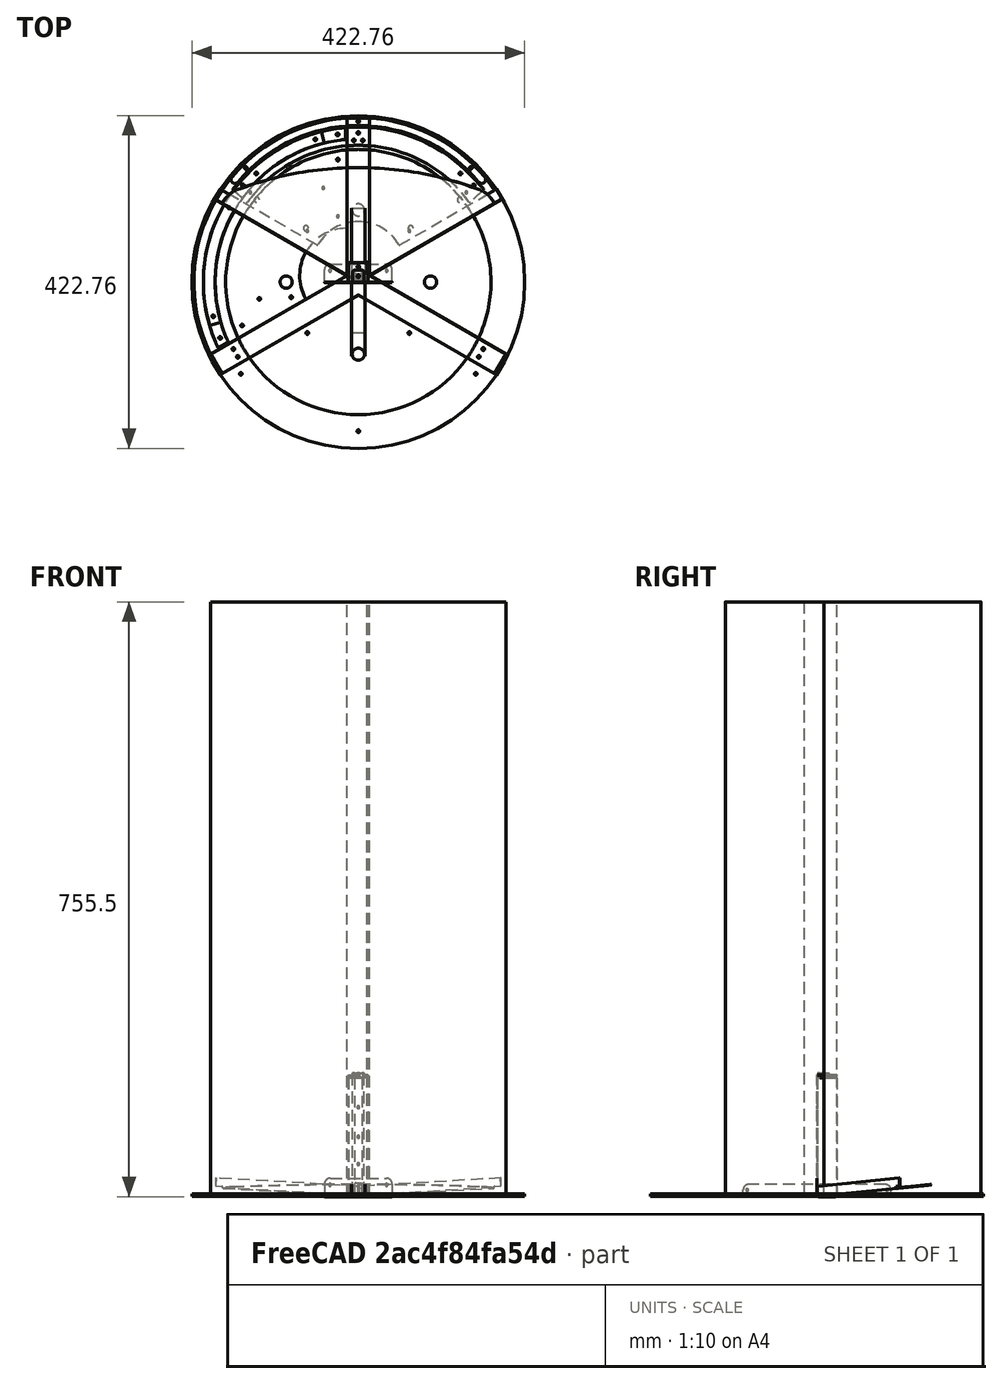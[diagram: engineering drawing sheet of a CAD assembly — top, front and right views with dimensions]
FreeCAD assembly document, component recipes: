
FREECAD ASSEMBLY — COMPONENT RECIPES ("composit_stand3-small")

This assembly document has 17 components, labeled P0..P16 below (a component is one placed body or linked part). 17 of them carry a construction recipe — the FreeCAD feature program that regenerates the part from scratch, quoted from this document or its linked companion documents; the rest are supplied as boundary geometry only. No exploded tour is included for this assembly.
NOTE — this tour is split across 2 documents so each fits a 32k-token context. This is document 1: the component sections continue in the remaining 1 document, each repeating the header above.
COMPONENT P0 — recipe-attached ("Body001_material_0.30ansi", modeled in this document).
Construction recipe (the document's own serialized feature program — sketch geometry with constraints, then the solid features built on it; lengths are millimeters unless a unit is written):

FEATURE [Sketcher::SketchObject] Sketch003
  FullyConstrained = true
  MapMode = 5
  Support = -> [XY_Plane001]
  sketch-geometry (13):
    g0: LineSegment StartX=-14.5 StartY=8.37158 StartZ=0 EndX=-14.5 EndY=208.372 EndZ=0
    g1: LineSegment StartX=-14.5 StartY=208.372 StartZ=0 EndX=14.5 EndY=208.372 EndZ=0
    g2: LineSegment StartX=187.705 StartY=-91.6284 StartZ=0 EndX=173.205 EndY=-116.743 EndZ=0
    g3: LineSegment StartX=173.205 StartY=-116.743 StartZ=0 EndX=0 EndY=-16.7432 EndZ=0
    g4: LineSegment StartX=0 StartY=-16.7432 StartZ=0 EndX=-173.205 EndY=-116.743 EndZ=0
    g5: LineSegment StartX=-173.205 StartY=-116.743 StartZ=0 EndX=-187.705 EndY=-91.6284 EndZ=0
    g6: LineSegment StartX=-187.705 StartY=-91.6284 StartZ=0 EndX=-14.5 EndY=8.37158 EndZ=0
    g7: LineSegment StartX=-14.5 StartY=8.37158 StartZ=0 EndX=0 EndY=0 EndZ=0
    g8: LineSegment StartX=0 StartY=0 StartZ=0 EndX=0 EndY=-16.7432 EndZ=0
    g9: LineSegment StartX=14.5 StartY=208.372 StartZ=0 EndX=14.5 EndY=8.97158 EndZ=0
    g10: LineSegment StartX=187.705 StartY=-91.6284 StartZ=0 EndX=11.5 EndY=10.1036 EndZ=0
    g11: LineSegment StartX=11.5 StartY=10.1036 StartZ=0 EndX=11.5 EndY=25.1036 EndZ=0
    g12: LineSegment StartX=0 StartY=0 StartZ=0 EndX=14.5 EndY=8.37158 EndZ=0
  constraints (40):
    c: Vertical(g0)
    c: Coincident(g0,g1)
    c: Coincident(g2,g3)
    c: PointOnObject(g3,g-2)
    c: Coincident(g3,g4)
    c: Coincident(g4,g5)
    c: Coincident(g6,g5)
    c: Equal(g4,g3)
    c: Equal(g2,g5)
    c: Equal(g5,g1)
    c: Perpendicular(g2,g3)
    c: Perpendicular(g5,g4)
    c: Perpendicular(g6,g5)
    c: Angle(g4,g3) = 2.0944
    c: Coincident(g7,g0)
    c: Coincident(g7,g-1)
    c: Coincident(g8,g7)
    c: Coincident(g8,g3)
    c: DistanceX(g1,g1) = 29
    c: DistanceY(g0) = 8.37158  'petal_conn_y'
    c: Coincident(g6,g0)
    c: Distance(g7,g1) = 208.875  'max_r'
    c: DistanceY(g7,g1) = 208.372  'total_petal_length'
    c: Coincident(g9,g1)
    c: Vertical(g9)
    c: Symmetric(g1,g0,g-2)
    c: Equal(g0,g6)
    c: Coincident(g10,g2)
    c: Coincident(g11,g10)
    c: Vertical(g11)
    c: Coincident(g12,g7)
    c: PointOnObject(g12,g10)
    c: PointOnObject(g12,g9)
    c: Equal(g12,g7)
    c: Equal(g7,g8)
    c: DistanceY(g0,g0) = 200
    c: Equal(g4,g6)
    c: DistanceY(g12,g9) = 0.6
    c: DistanceX(g10,g12) = 3
    c: DistanceY(g10,g11) = 15
FEATURE [PartDesign::CoordinateSystem] Local_CS
  AttacherType = Attacher::AttachEngine3D
  AttachmentOffset = pos=(0,8.37158,0) rot=(0,0,1;0rad)
  MapMode = 5
  Placement = pos=(0,8.37158,0) rot=(0,0,1;0rad)
  Support = -> [XY_Plane001]
FEATURE [PartDesign::Plane] DatumPlane001
  AttachmentOffset = pos=(0,0,-100) rot=(0,0,1;0rad)
  Length = 484.686
  MapMode = 3
  Placement = pos=(0,108.372,-2.22e-14) rot=(1,0,0;1.5708rad)
  ResizeMode = 0
  Support = -> [Local_CS]
  Width = 908.503
FEATURE [Sketcher::SketchObject] Sketch005
  AttachmentOffset = pos=(14.5,8.37158,0) rot=(0,0,1;0rad)
  FullyConstrained = true
  MapMode = 5
  Placement = pos=(14.5,8.37158,0) rot=(0,0,1;0rad)
  Support = -> [XY_Plane001]
  sketch-geometry (4):
    g0: LineSegment StartX=0 StartY=0 StartZ=0 EndX=-3 EndY=0 EndZ=0
    g1: LineSegment StartX=-3 StartY=0 StartZ=0 EndX=-3 EndY=3.1 EndZ=0
    g2: LineSegment StartX=-3 StartY=3.1 StartZ=0 EndX=0 EndY=0.1 EndZ=0
    g3: LineSegment StartX=0 StartY=0.1 StartZ=0 EndX=0 EndY=0 EndZ=0
  constraints (11):
    c: Coincident(g0,g1)
    c: Coincident(g1,g2)
    c: Coincident(g2,g3)
    c: Coincident(g3,g0)
    c: Horizontal(g0)
    c: Vertical(g1)
    c: Vertical(g3)
    c: Coincident(g0,g-1)
    c: DistanceY(g2) = 0.1
    c: Angle(g-1,g2) = 2.35619
    c: DistanceX(g0,g0) = 3
FEATURE [Sketcher::SketchObject] Sketch009
  FullyConstrained = true
  MapMode = 5
  Placement = pos=(0,0,0) rot=(0.57735,0.57735,0.57735;2.0944rad)
  Support = -> [YZ_Plane001]
  sketch-geometry (18):
    g0: LineSegment StartX=0 StartY=0 StartZ=0 EndX=0 EndY=157 EndZ=0
    g1: LineSegment StartX=192.75 StartY=152 StartZ=0 EndX=192.75 EndY=127 EndZ=0
    g2: LineSegment StartX=187.75 StartY=122 StartZ=0 EndX=183.66 EndY=122 EndZ=0
    g3: LineSegment StartX=178.808 StartY=118.205 StartZ=0 EndX=149.45 EndY=0 EndZ=0
    g4: LineSegment StartX=149.45 StartY=0 StartZ=0 EndX=0 EndY=0 EndZ=0
    g5: ArcOfCircle CenterX=187.75 CenterY=152 CenterZ=0 NormalX=0 NormalY=0 NormalZ=1 AngleXU=0 Radius=5 StartAngle=2.5e-15 EndAngle=1.5708
    g6: GeomPoint X=192.75 Y=157 Z=0
    g7: ArcOfCircle CenterX=187.75 CenterY=127 CenterZ=0 NormalX=0 NormalY=0 NormalZ=1 AngleXU=0 Radius=5 StartAngle=4.71239 EndAngle=6.28319
    g8: GeomPoint X=192.75 Y=122 Z=0
    g9: ArcOfCircle CenterX=183.66 CenterY=117 CenterZ=0 NormalX=0 NormalY=0 NormalZ=1 AngleXU=0 Radius=5 StartAngle=1.5708 EndAngle=2.89816
    g10: GeomPoint X=179.75 Y=122 Z=0
    g11: LineSegment StartX=73 StartY=116.5 StartZ=0 EndX=166 EndY=116.5 EndZ=0
    g12: LineSegment StartX=166 StartY=116.5 StartZ=0 EndX=166 EndY=157 EndZ=0
    g13: LineSegment StartX=166 StartY=157 StartZ=0 EndX=73 EndY=157 EndZ=0
    g14: LineSegment StartX=73 StartY=157 StartZ=0 EndX=73 EndY=116.5 EndZ=0
    g15: LineSegment StartX=0 StartY=157 StartZ=0 EndX=73 EndY=157 EndZ=0
    g16: LineSegment StartX=166 StartY=157 StartZ=0 EndX=187.75 EndY=157 EndZ=0
    g17: LineSegment StartX=208.395 StartY=149.752 StartZ=0 EndX=192.75 EndY=149.752 EndZ=0
  constraints (47):
    c: Coincident(g-1,g0)
    c: Vertical(g0)
    c: Vertical(g1)
    c: Horizontal(g2)
    c: PointOnObject(g3,g-1)
    c: Coincident(g3,g4)
    c: Coincident(g4,g0)
    c: Distance(g0,g6) = 192.75
    c: DistanceY(g8,g6) = 35
    c: DistanceX(g4,g4) = 149.45
    c: DistanceY(g0,g0) = 157
    c: PointOnObject(g6,g1)
    c: Tangent(g1,g5) = 1.5708
    c: PointOnObject(g8,g2)
    c: PointOnObject(g8,g1)
    c: Tangent(g2,g7) = 1.5708
    c: Tangent(g1,g7) = 1.5708
    c: PointOnObject(g10,g3)
    c: PointOnObject(g10,g2)
    c: Tangent(g3,g9) = -1.5708
    c: Tangent(g2,g9) = -1.5708
    c: Equal(g9,g7)
    c: Equal(g7,g5)
    c: Diameter(g7) = 10
    c: Distance(g8,g10) = 13
    c: Coincident(g11,g12)
    c: Coincident(g12,g13)
    c: Coincident(g13,g14)
    c: Coincident(g14,g11)
    c: Horizontal(g11)
    c: Horizontal(g13)
    c: Vertical(g12)
    c: Vertical(g14)
    c: DistanceX(g11,g11) = 93  'length'
    c: DistanceY(g14,g14) = 40.5  'height'
    c: DistanceX(g11) = 73
    c: DistanceY(g13) = 157
    c: Coincident(g15,g0)
    c: Coincident(g15,g13)
    c: Coincident(g16,g12)
    c: Horizontal(g16)
    c: Tangent(g16,g5) = 1.5708
    c: PointOnObject(g6,g16)
    c: PointOnObject(g17,g1)
    c: Horizontal(g17)
    c: DistanceX(g17) = 208.395
    c: DistanceY(g17) = 149.752
FEATURE [PartDesign::Plane] DatumPlane002
  AttachmentOffset = pos=(0,0,407) rot=(0,0,1;0rad)
  Length = 445.022
  MapMode = 5
  Placement = pos=(0,0,407) rot=(0,0,1;0rad)
  ResizeMode = 0
  Support = -> [XY_Plane001]
  Width = 394.84
FEATURE [Sketcher::SketchObject] Sketch012
  FullyConstrained = true
  MapMode = 5
  Placement = pos=(0,0,0) rot=(0.57735,0.57735,0.57735;2.0944rad)
  Support = -> [YZ_Plane001]
  sketch-geometry (8):
    g0: LineSegment StartX=0 StartY=0 StartZ=0 EndX=50 EndY=0 EndZ=0
    g1: LineSegment StartX=50 StartY=0 StartZ=0 EndX=50 EndY=263 EndZ=0
    g2: LineSegment StartX=50 StartY=263 StartZ=0 EndX=0 EndY=263 EndZ=0
    g3: LineSegment StartX=0 StartY=263 StartZ=0 EndX=0 EndY=0 EndZ=0
    g4: LineSegment StartX=0 StartY=774 StartZ=0 EndX=50 EndY=774 EndZ=0
    g5: LineSegment StartX=50 StartY=774 StartZ=0 EndX=50 EndY=724 EndZ=0
    g6: LineSegment StartX=50 StartY=724 StartZ=0 EndX=0 EndY=724 EndZ=0
    g7: LineSegment StartX=0 StartY=724 StartZ=0 EndX=0 EndY=774 EndZ=0
  constraints (23):
    c: Coincident(g0,g1)
    c: Coincident(g1,g2)
    c: Coincident(g2,g3)
    c: Coincident(g3,g0)
    c: Horizontal(g0)
    c: Horizontal(g2)
    c: Vertical(g1)
    c: Vertical(g3)
    c: Coincident(g0,g-1)
    c: Distance(g0) = 50
    c: DistanceY(g2) = 263
    c: Coincident(g4,g5)
    c: Coincident(g5,g6)
    c: Coincident(g6,g7)
    c: Coincident(g7,g4)
    c: Horizontal(g4)
    c: Horizontal(g6)
    c: Vertical(g5)
    c: Vertical(g7)
    c: PointOnObject(g4,g-2)
    c: Vertical(g5,g1)
    c: DistanceY(g4) = 774
    c: DistanceY(g7,g7) = 50
FEATURE [Sketcher::SketchObject] Sketch013
  AttachmentOffset = pos=(0,157,0) rot=(0,0,1;0rad)
  FullyConstrained = true
  MapMode = 5
  Placement = pos=(-3.49e-14,3.49e-14,157) rot=(0.57735,0.57735,0.57735;2.0944rad)
  Support = -> [YZ_Plane001]
  sketch-geometry (7):
    g0: LineSegment StartX=75 StartY=0 StartZ=0 EndX=0 EndY=0 EndZ=0
    g1: LineSegment StartX=0 StartY=0 StartZ=0 EndX=0 EndY=60 EndZ=0
    g2: LineSegment StartX=0 StartY=60 StartZ=0 EndX=30 EndY=60 EndZ=0
    g3: LineSegment StartX=35 StartY=55 StartZ=0 EndX=35 EndY=40 EndZ=0
    g4: ArcOfCircle CenterX=75 CenterY=40 CenterZ=0 NormalX=0 NormalY=0 NormalZ=1 AngleXU=0 Radius=40 StartAngle=3.14159 EndAngle=4.71239
    g5: ArcOfCircle CenterX=30 CenterY=55 CenterZ=0 NormalX=0 NormalY=0 NormalZ=1 AngleXU=0 Radius=5 StartAngle=2e-16 EndAngle=1.5708
    g6: GeomPoint X=35 Y=60 Z=0
  constraints (18):
    c: PointOnObject(g0,g-1)
    c: Coincident(g0,g-1)
    c: Coincident(g0,g1)
    c: PointOnObject(g1,g-2)
    c: Coincident(g1,g2)
    c: Horizontal(g2)
    c: Vertical(g3)
    c: PointOnObject(g6,g2)
    c: PointOnObject(g6,g3)
    c: Tangent(g2,g5) = 1.5708
    c: Tangent(g3,g5) = 1.5708
    c: Diameter(g4) = 80
    c: Tangent(g4,g3) = -1.5708
    c: Distance(g1) = 60
    c: Tangent(g4,g0) = 1.5708
    c: Diameter(g5) = 10
    c: DistanceX(g3) = 35
    c: Distance(g0) = 75
FEATURE [PartDesign::CoordinateSystem] Local_CS008
  AttacherType = Attacher::AttachEngine3D
  MapMode = 5
  Support = -> [XY_Plane001]
FEATURE [PartDesign::CoordinateSystem] Local_CS011
  AttacherType = Attacher::AttachEngine3D
  AttachmentOffset = pos=(0,100,0) rot=(0,0,1;0rad)
  MapMode = 5
  Placement = pos=(0,108.372,0) rot=(0,0,1;0rad)
  Support = -> [Local_CS]
FEATURE [PartDesign::Plane] DatumPlane
  Length = 426.918
  MapMode = 4
  Placement = pos=(0,108.372,0) rot=(0.57735,0.57735,0.57735;2.0944rad)
  ResizeMode = 0
  Support = -> [Local_CS011]
  Width = 900.917
FEATURE [Sketcher::SketchObject] Sketch011
  AttachmentOffset = pos=(-88,277,0) rot=(0,0,1;0rad)
  FullyConstrained = true
  MapMode = 5
  Placement = pos=(0,20.3716,277) rot=(0.57735,0.57735,0.57735;2.0944rad)
  Support = -> [DatumPlane]
  sketch-geometry (1):
    g0: Circle CenterX=0 CenterY=0 CenterZ=0 NormalX=0 NormalY=0 NormalZ=1 AngleXU=0 Radius=1.7
  constraints (2):
    c: Coincident(g0,g-1)
    c: Diameter(g0) = 3.4
FEATURE [PartDesign::Plane] DatumPlane011
  AttachmentOffset = pos=(0,0,0) rot=(0,0,1;0.523599rad)
  Length = 583.048
  MapMode = 5
  Placement = pos=(0,0,0) rot=(0,0,1;0.523599rad)
  ResizeMode = 0
  Support = -> [XY_Plane001]
  Width = 564.68
FEATURE [PartDesign::SubShapeBinder] Binder027
  BindCopyOnChange = 0
  BindMode = 0
  ClaimChildren = false
  Context = -> Model [Body001001.Binder027.Edge3]
  Fuse = false
  MakeFace = true
  OffsetFill = false
  OffsetIntersection = false
  OffsetJoinType = 0
  OffsetOpenResult = false
  PartialLoad = false
  Placement = pos=(0,108.372,229) rot=(0.57735,0.57735,0.57735;2.0944rad)
  Relative = true
  _Version = 2
FEATURE [PartDesign::CoordinateSystem] Local_CS035
  AttacherType = Attacher::AttachEngine3D
  AttachmentOffset = pos=(0,0,774) rot=(0,0,1;0rad)
  MapMode = 5
  Placement = pos=(0,108.372,774) rot=(0,0,1;0rad)
  Support = -> [Local_CS011]
FEATURE [PartDesign::CoordinateSystem] Local_CS036  label="droppers_center"
  AttacherType = Attacher::AttachEngine3D
  AttachmentOffset = pos=(0,0,-19) rot=(0,0,1;0rad)
  MapMode = 5
  Placement = pos=(0,108.372,755) rot=(0,0,1;0rad)
  Support = -> [Local_CS035]
FEATURE [PartDesign::CoordinateSystem] Local_CS037  label="gutter_fixture_center"
  AttacherType = Attacher::AttachEngine3D
  AttachmentOffset = pos=(0,0,-12) rot=(0,0,1;0rad)
  MapMode = 5
  Placement = pos=(0,108.372,743) rot=(0,0,1;0rad)
  Support = -> [Local_CS036]
FEATURE [PartDesign::CoordinateSystem] Local_CS038  label="modules_top_center"
  AttacherType = Attacher::AttachEngine3D
  AttachmentOffset = pos=(0,0,-5) rot=(0,0,1;0rad)
  MapMode = 5
  Placement = pos=(0,108.372,738) rot=(0,0,1;0rad)
  Support = -> [Local_CS037]
FEATURE [Sketcher::SketchObject] Sketch112
  FullyConstrained = true
  MapMode = 5
  Placement = pos=(0,0,0) rot=(0.57735,0.57735,0.57735;2.0944rad)
  Support = -> [YZ_Plane001]
  sketch-geometry (5):
    g0: LineSegment StartX=-6.5 StartY=-3.5 StartZ=0 EndX=-6.5 EndY=3.5 EndZ=0
    g1: LineSegment StartX=-6.5 StartY=3.5 StartZ=0 EndX=6.5 EndY=3.5 EndZ=0
    g2: LineSegment StartX=6.5 StartY=3.5 StartZ=0 EndX=6.5 EndY=-3.5 EndZ=0
    g3: LineSegment StartX=6.5 StartY=-3.5 StartZ=0 EndX=-6.5 EndY=-3.5 EndZ=0
    g4: GeomPoint X=0 Y=0 Z=0
  constraints (12):
    c: Coincident(g0,g1)
    c: Coincident(g1,g2)
    c: Coincident(g2,g3)
    c: Coincident(g3,g0)
    c: Horizontal(g1)
    c: Horizontal(g3)
    c: Vertical(g0)
    c: Vertical(g2)
    c: Symmetric(g1,g0,g4)
    c: Coincident(g4,g-1)
    c: DistanceX(g1,g1) = 13
    c: DistanceY(g2,g2) = 7
FEATURE [Sketcher::SketchObject] Sketch113
  FullyConstrained = true
  MapMode = 5
  Placement = pos=(0,0,0) rot=(0.57735,0.57735,0.57735;2.0944rad)
  Support = -> [YZ_Plane001]
  sketch-geometry (8):
    g0: ArcOfCircle CenterX=0 CenterY=0 CenterZ=0 NormalX=0 NormalY=0 NormalZ=1 AngleXU=0 Radius=12.625 StartAngle=3.14159 EndAngle=6.28319
    g1: LineSegment StartX=12.625 StartY=-3.1e-15 StartZ=0 EndX=12.625 EndY=12.5 EndZ=0
    g2: LineSegment StartX=-12.625 StartY=1.5e-15 StartZ=0 EndX=-12.625 EndY=12.5 EndZ=0
    g3: ArcOfCircle CenterX=15.125 CenterY=12.5 CenterZ=0 NormalX=0 NormalY=0 NormalZ=1 AngleXU=0 Radius=2.5 StartAngle=1.5708 EndAngle=3.14159
    g4: ArcOfCircle CenterX=-15.125 CenterY=12.5 CenterZ=0 NormalX=0 NormalY=0 NormalZ=1 AngleXU=0 Radius=2.5 StartAngle=0 EndAngle=1.5708
    g5: LineSegment StartX=-15.125 StartY=15 StartZ=0 EndX=-15.125 EndY=19 EndZ=0
    g6: LineSegment StartX=-15.125 StartY=19 StartZ=0 EndX=15.125 EndY=19 EndZ=0
    g7: LineSegment StartX=15.125 StartY=19 StartZ=0 EndX=15.125 EndY=15 EndZ=0
  constraints (24):
    c: Coincident(g0,g-1)
    c: PointOnObject(g0,g-1)
    c: PointOnObject(g0,g-1)
    c: Coincident(g1,g0)
    c: Vertical(g1)
    c: Coincident(g2,g0)
    c: Vertical(g2)
    c: Coincident(g5,g4)
    c: Vertical(g5)
    c: Coincident(g6,g5)
    c: Horizontal(g6)
    c: Coincident(g7,g6)
    c: Coincident(g7,g3)
    c: Vertical(g7)
    c: Perpendicular(g3,g7)
    c: Tangent(g3,g1) = 1.5708
    c: Tangent(g4,g2) = -1.5708
    c: Perpendicular(g4,g5)
    c: Diameter(g0) = 25.25
    c: Distance(g0,g6) = 19
    c: Equal(g4,g3)
    c: Diameter(g4) = 5
    c: DistanceY(g7,g7) = 4
    c: Equal(g5,g7)
FEATURE [PartDesign::SubShapeBinder] Binder032
  BindCopyOnChange = 0
  BindMode = 0
  ClaimChildren = false
  Context = -> Body001 [Binder032.]
  Fuse = false
  MakeFace = true
  OffsetFill = false
  OffsetIntersection = false
  OffsetJoinType = 0
  OffsetOpenResult = false
  PartialLoad = false
  Placement = pos=(0,108.372,755) rot=(0,0,1;0rad)
  Relative = true
  Support = -> [Array001]
  _Version = 2
FEATURE [PartDesign::SubShapeBinder] Binder033
  BindCopyOnChange = 0
  BindMode = 0
  ClaimChildren = false
  Context = -> Body001 [Binder033.]
  Fuse = false
  MakeFace = true
  OffsetFill = false
  OffsetIntersection = false
  OffsetJoinType = 0
  OffsetOpenResult = false
  PartialLoad = false
  Placement = pos=(0,108.372,755) rot=(0,0,1;0rad)
  Relative = true
  Support = -> [Array002]
  _Version = 2
FEATURE [PartDesign::SubShapeBinder] Binder034
  BindCopyOnChange = 0
  BindMode = 0
  ClaimChildren = false
  Context = -> Body001 [Binder034.]
  Fuse = false
  MakeFace = true
  OffsetFill = false
  OffsetIntersection = false
  OffsetJoinType = 0
  OffsetOpenResult = false
  PartialLoad = false
  Placement = pos=(0,108.372,738) rot=(0,0,1;0rad)
  Relative = true
  Support = -> [Array]
  _Version = 2
FEATURE [Sketcher::SketchObject] Sketch114
  FullyConstrained = true
  MapMode = 5
  Placement = pos=(0,0,0) rot=(0.57735,0.57735,0.57735;2.0944rad)
  Support = -> [YZ_Plane001]
  sketch-geometry (1):
    g0: Circle CenterX=0 CenterY=0 CenterZ=0 NormalX=0 NormalY=0 NormalZ=1 AngleXU=0 Radius=1.7
  constraints (2):
    c: Coincident(g0,g-1)
    c: Diameter(g0) = 3.4
FEATURE [PartDesign::SubShapeBinder] Binder035
  BindCopyOnChange = 0
  BindMode = 0
  ClaimChildren = false
  Context = -> Body001 [Binder035.]
  Fuse = false
  MakeFace = true
  OffsetFill = false
  OffsetIntersection = false
  OffsetJoinType = 0
  OffsetOpenResult = false
  PartialLoad = false
  Placement = pos=(0,108.372,743) rot=(0,0,1;0rad)
  Relative = true
  Support = -> [Array003]
  _Version = 2
FEATURE [Sketcher::SketchObject] Sketch119
  AttachmentOffset = pos=(180,12.5,0) rot=(0,0,1;0rad)
  FullyConstrained = true
  MapMode = 5
  Placement = pos=(3.72e-14,180,12.5) rot=(0.57735,0.57735,0.57735;2.0944rad)
  Support = -> [YZ_Plane001]
  sketch-geometry (1):
    g0: Circle CenterX=0 CenterY=0 CenterZ=0 NormalX=0 NormalY=0 NormalZ=1 AngleXU=0 Radius=1.7
  constraints (2):
    c: Coincident(g0,g-1)
    c: Diameter(g0) = 3.4
FEATURE [PartDesign::CoordinateSystem] Local_CS039
  AttacherType = Attacher::AttachEngine3D
  AttachmentOffset = pos=(119.5,154,11.5) rot=(0,0.707107,0.707107;3.14159rad)
  MapMode = 5
  Placement = pos=(11.5,119.5,154) rot=(0,0,1;4.71239rad)
  Support = -> [YZ_Plane001]
FEATURE [Sketcher::SketchObject] Sketch125
  AttachmentOffset = pos=(0,25,0) rot=(0,0,1;0rad)
  FullyConstrained = true
  MapMode = 5
  Placement = pos=(0,-5.6e-15,25) rot=(1,0,0;1.5708rad)
  Support = -> [XZ_Plane001]
  sketch-geometry (1):
    g0: Circle CenterX=0 CenterY=0 CenterZ=0 NormalX=0 NormalY=0 NormalZ=1 AngleXU=0 Radius=7
  constraints (2):
    c: Coincident(g0,g-1)
    c: Diameter(g0) = 14
FEATURE [Sketcher::SketchObject] Sketch128
  FullyConstrained = true
  MapMode = 5
  Placement = pos=(0,0,0) rot=(0.57735,0.57735,0.57735;2.0944rad)
  Support = -> [YZ_Plane001]
  sketch-geometry (4):
    g0: LineSegment StartX=73 StartY=116.5 StartZ=0 EndX=166 EndY=116.5 EndZ=0
    g1: LineSegment StartX=166 StartY=116.5 StartZ=0 EndX=166 EndY=157 EndZ=0
    g2: LineSegment StartX=166 StartY=157 StartZ=0 EndX=73 EndY=157 EndZ=0
    g3: LineSegment StartX=73 StartY=157 StartZ=0 EndX=73 EndY=116.5 EndZ=0
  constraints (12):
    c: Coincident(g0,g1)
    c: Coincident(g1,g2)
    c: Coincident(g2,g3)
    c: Coincident(g3,g0)
    c: Horizontal(g0)
    c: Horizontal(g2)
    c: Vertical(g1)
    c: Vertical(g3)
    c: DistanceX(g0,g0) = 93  'length'
    c: DistanceY(g3,g3) = 40.5  'height'
    c: DistanceX(g0) = 73  'offset_x'
    c: DistanceY(g2) = 157
FEATURE [Sketcher::SketchObject] Sketch129
  AttachmentOffset = pos=(0,0,0) rot=(0,1,0;3.66519rad)
  FullyConstrained = true
  MapMode = 5
  Placement = pos=(0,0,0) rot=(-0.186157,0.694747,0.694747;3.50969rad)
  Support = -> [XZ_Plane001]
  sketch-geometry (9):
    g0: LineSegment StartX=0 StartY=0 StartZ=0 EndX=169.18 EndY=0 EndZ=0
    g1: LineSegment StartX=169.18 StartY=0 StartZ=0 EndX=169.18 EndY=157 EndZ=0
    g2: LineSegment StartX=0 StartY=157 StartZ=0 EndX=0 EndY=0 EndZ=0
    g3: LineSegment StartX=73 StartY=116.5 StartZ=0 EndX=166 EndY=116.5 EndZ=0
    g4: LineSegment StartX=166 StartY=116.5 StartZ=0 EndX=166 EndY=157 EndZ=0
    g5: LineSegment StartX=166 StartY=157 StartZ=0 EndX=73 EndY=157 EndZ=0
    g6: LineSegment StartX=73 StartY=157 StartZ=0 EndX=73 EndY=116.5 EndZ=0
    g7: LineSegment StartX=169.18 StartY=157 StartZ=0 EndX=166 EndY=157 EndZ=0
    g8: LineSegment StartX=73 StartY=157 StartZ=0 EndX=0 EndY=157 EndZ=0
  constraints (25):
    c: Coincident(g0,g1)
    c: Coincident(g1,g7)
    c: Coincident(g8,g2)
    c: Coincident(g2,g0)
    c: Horizontal(g0)
    c: Vertical(g1)
    c: Vertical(g2)
    c: Coincident(g0,g-1)
    c: DistanceY(g8) = 157
    c: Coincident(g3,g4)
    c: Coincident(g4,g5)
    c: Coincident(g5,g6)
    c: Coincident(g6,g3)
    c: Horizontal(g3)
    c: Horizontal(g5)
    c: Vertical(g4)
    c: Vertical(g6)
    c: DistanceX(g3,g3) = 93  'length'
    c: DistanceY(g6,g6) = 40.5  'height'
    c: DistanceX(g3) = 73
    c: DistanceY(g5) = 157
    c: Horizontal(g7)
    c: Coincident(g8,g5)
    c: Coincident(g7,g4)
    c: DistanceX(g7,g7) = 3.18
FEATURE [PartDesign::CoordinateSystem] Local_CS041
  AttacherType = Attacher::AttachEngine3D
  AttachmentOffset = pos=(119.5,157,14.5) rot=(0,0.707107,0.707107;3.14159rad)
  MapMode = 5
  Placement = pos=(14.5,119.5,157) rot=(0,0,1;4.71239rad)
  Support = -> [YZ_Plane001]
FEATURE [Sketcher::SketchObject] Sketch130
  AttachmentOffset = pos=(0,40,0) rot=(0,0,1;0rad)
  FullyConstrained = true
  MapMode = 5
  Placement = pos=(54.5,119.5,157) rot=(0,0,-1;1.5708rad)
  Support = -> [Local_CS041]
  sketch-geometry (6):
    g0: ArcOfCircle CenterX=36.5 CenterY=-10 CenterZ=0 NormalX=0 NormalY=0 NormalZ=1 AngleXU=0 Radius=10 StartAngle=6.28318 EndAngle=7.85398
    g1: ArcOfCircle CenterX=-36.5 CenterY=-10 CenterZ=0 NormalX=0 NormalY=0 NormalZ=1 AngleXU=0 Radius=10 StartAngle=1.5708 EndAngle=3.14159
    g2: LineSegment StartX=-46.5 StartY=-10 StartZ=0 EndX=-46.5 EndY=0 EndZ=0
    g3: LineSegment StartX=-36.5 StartY=0 StartZ=0 EndX=-46.5 EndY=0 EndZ=0
    g4: LineSegment StartX=46.5 StartY=-10 StartZ=0 EndX=46.5 EndY=0 EndZ=0
    g5: LineSegment StartX=36.5 StartY=0 StartZ=0 EndX=46.5 EndY=0 EndZ=0
  constraints (17):
    c: PointOnObject(g0,g-1)
    c: PointOnObject(g1,g-1)
    c: Coincident(g2,g1)
    c: PointOnObject(g2,g-1)
    c: Vertical(g2)
    c: Tangent(g2,g1)
    c: Coincident(g3,g2)
    c: Coincident(g4,g0)
    c: PointOnObject(g4,g-1)
    c: Vertical(g4)
    c: Tangent(g4,g0)
    c: Coincident(g5,g4)
    c: Tangent(g5,g0) = 1.5708
    c: Tangent(g3,g1) = -1.5708
    c: DistanceX(g2,g4) = 93
    c: Symmetric(g1,g0,g-2)
    c: Diameter(g0) = 20
FEATURE [PartDesign::CoordinateSystem] Local_CS042
  AttacherType = Attacher::AttachEngine3D
  AttachmentOffset = pos=(0,0,0) rot=(0,0,1;2.0944rad)
  MapMode = 5
  Placement = pos=(0,0,0) rot=(0,0,1;2.0944rad)
  Support = -> [XY_Plane001]
FEATURE [PartDesign::CoordinateSystem] Local_CS012
  AttacherType = Attacher::AttachEngine3D
  AttachmentOffset = pos=(14.5,119.5,157) rot=(0,0,1;4.71239rad)
  MapMode = 5
  Placement = pos=(-110.74,-47.1926,157) rot=(0,0,-1;5.75959rad)
  Support = -> [Local_CS042]
FEATURE [PartDesign::Plane] DatumPlane012
  Length = 583.048
  MapMode = 5
  Placement = pos=(-110.74,-47.1926,157) rot=(0,0,1;0.523599rad)
  ResizeMode = 0
  Support = -> [Local_CS012]
  Width = 564.68
FEATURE [PartDesign::FeaturePython] BaseBend011  # WARN: FeaturePython — macro-defined, semantics opaque (R4)
  BendSide = 0
  BendSketch = -> Sketch003
  MidPlane = false
  Reverse = false
  length = 755
  radius = 0.01
  thickness = 0.3
  expr: length = <<main>>.total_length
  expr: radius = <<main>>.bend_r
  expr: thickness = 0.3mm
FEATURE [PartDesign::Body] Body001  label="Body001_material_0.30ansi"
  Group = -> [BaseBend011,Local_CS,Local_CS011,Sketch003,Local_CS012,DatumPlane011,DatumPlane012,Local_CS035,Local_CS036,Local_CS037,Local_CS038,Sketch112,Sketch113,Sketch128,Local_CS039,Sketch129,Local_CS041,Sketch130,Local_CS042,DatumPlane,DatumPlane001,Sketch005,Binder032,Binder033,Binder034,Binder035,Binder027,Sketch119,Sketch125,Sketch114,Sketch009,Sketch011,DatumPlane002,Sketch012,Sketch013,Local_CS008,+17 more]
  Origin = -> Origin001
  Tip = -> BaseBend011
COMPONENT P1 — recipe-attached ("basin_cover", modeled in this document).
Construction recipe (the document's own serialized feature program — sketch geometry with constraints, then the solid features built on it; lengths are millimeters unless a unit is written):

FEATURE [Sketcher::SketchObject] Sketch047
  FullyConstrained = true
  MapMode = 5
  Support = -> [XY_Plane015]
  sketch-geometry (8):
    g0: ArcOfCircle CenterX=0 CenterY=16.7432 CenterZ=0 NormalX=0 NormalY=0 NormalZ=1 AngleXU=0 Radius=60 StartAngle=0.539993 EndAngle=1.5708
    g1: ArcOfCircle CenterX=52.3205 CenterY=48.1051 CenterZ=0 NormalX=0 NormalY=0 NormalZ=1 AngleXU=0 Radius=1 StartAngle=3.68159 EndAngle=5.23599
    g2: LineSegment StartX=52.8205 StartY=47.2391 StartZ=0 EndX=172.274 EndY=116.206 EndZ=0
    g3: ArcOfCircle CenterX=171.774 CenterY=117.072 CenterZ=0 NormalX=0 NormalY=0 NormalZ=1 AngleXU=0 Radius=1 StartAngle=5.23599 EndAngle=6.88142
    g4: ArcOfCircle CenterX=0 CenterY=0 CenterZ=0 NormalX=0 NormalY=0 NormalZ=1 AngleXU=0 Radius=208.875 StartAngle=0.598232 EndAngle=1.5708
    g5: LineSegment StartX=3.7e-15 StartY=76.7432 StartZ=0 EndX=1.28e-14 EndY=208.875 EndZ=0
    g6: LineSegment StartX=52.8205 StartY=47.2391 StartZ=0 EndX=0 EndY=16.7432 EndZ=0
    g7: GeomPoint X=173.205 Y=116.743 Z=0
  constraints (22):
    c: PointOnObject(g0,g-2)
    c: PointOnObject(g4,g-2)
    c: Diameter(g1) = 2
    c: Diameter(g3) = 2
    c: Tangent(g1,g0) = 1.5708
    c: Tangent(g3,g2) = -1.5708
    c: Angle(g2,g-1) = 2.61799
    c: Coincident(g5,g0)
    c: Coincident(g5,g4)
    c: Tangent(g1,g2) = -1.5708
    c: Coincident(g6,g1)
    c: Tangent(g6,g2)
    c: Coincident(g6,g0)
    c: Diameter(g0) = 120
    c: PointOnObject(g7,g4)
    c: PointOnObject(g7,g2)
    c: DistanceY(g4) = 208.875
    c: Distance(g4,g0) = 16.7432  'major_r_offset'
    c: Coincident(g4,g-1)
    c: PointOnObject(g0,g-2)
    c: Distance(g0,g7) = 200
    c: Tangent(g3,g4) = -1.5708
FEATURE [PartDesign::Pad] Pad012
  Direction = (0,0,1)
  Length = 3
  Length2 = 10
  Profile = -> Sketch047
  ReferenceAxis = -> Sketch047 [N_Axis]
  Type = 0
FEATURE [PartDesign::CoordinateSystem] Local_CS013
  AttacherType = Attacher::AttachEngine3D
  MapMode = 5
  Support = -> [XY_Plane015]
FEATURE [PartDesign::CoordinateSystem] Local_CS016
  AttacherType = Attacher::AttachEngine3D
  AttachmentOffset = pos=(0,0,0) rot=(0,0,1;0.523599rad)
  MapMode = 5
  Placement = pos=(0,0,0) rot=(0,0,1;0.523599rad)
  Support = -> [XY_Plane015]
FEATURE [PartDesign::Plane] DatumPlane015
  Length = 81.9615
  MapMode = 5
  Placement = pos=(0,0,0) rot=(0,0,1;0.523599rad)
  ResizeMode = 0
  Support = -> [Local_CS016]
  Width = 81.9615
FEATURE [PartDesign::Plane] DatumPlane016
  Length = 79.989
  MapMode = 4
  Placement = pos=(86.82,84.1932,0) rot=(0.377964,0.654654,0.654654;2.41886rad)
  ResizeMode = 0
  Width = 61.6877
FEATURE [PartDesign::CoordinateSystem] Local_CS026
  AttacherType = Attacher::AttachEngine3D
  AttachmentOffset = pos=(0,16.7432,0) rot=(0,0,1;0.523599rad)
  MapMode = 5
  Placement = pos=(0,16.7432,0) rot=(0,0,1;0.523599rad)
  Support = -> [XY_Plane015]
FEATURE [PartDesign::SubShapeBinder] Binder041
  BindCopyOnChange = 0
  BindMode = 0
  ClaimChildren = false
  Context = -> Model [Body001003005002.Binder041.]
  Fuse = false
  MakeFace = true
  OffsetFill = false
  OffsetIntersection = false
  OffsetJoinType = 0
  OffsetOpenResult = false
  PartialLoad = false
  Relative = false
  Support = -> [Body001003005003013[Pocket041.Sketch083.]]
  _Version = 2
FEATURE [PartDesign::SubShapeBinder] Binder042
  BindCopyOnChange = 0
  BindMode = 0
  ClaimChildren = false
  Context = -> Model [Body001003005002.Binder042.]
  Fuse = false
  MakeFace = true
  OffsetFill = false
  OffsetIntersection = false
  OffsetJoinType = 0
  OffsetOpenResult = false
  PartialLoad = false
  Relative = false
  Support = -> [Body001003005003013[Pocket042.Sketch084.]]
  _Version = 2
FEATURE [PartDesign::SubShapeBinder] Binder043
  BindCopyOnChange = 0
  BindMode = 0
  ClaimChildren = false
  Context = -> Model [Body001003005002.Binder043.]
  Fuse = false
  MakeFace = true
  OffsetFill = false
  OffsetIntersection = false
  OffsetJoinType = 0
  OffsetOpenResult = false
  PartialLoad = false
  Placement = pos=(89.24,84.4317,0) rot=(0,0,1;0.523599rad)
  Relative = false
  Support = -> [Body001[Sketch043.]]
  _Version = 2
FEATURE [PartDesign::CoordinateSystem] Local_CS043
  AttacherType = Attacher::AttachEngine3D
  AttachmentOffset = pos=(119.5,28.5,0) rot=(0,0,1;0rad)
  MapMode = 5
  Placement = pos=(89.24,84.4317,0) rot=(0,0,1;0.523599rad)
  Support = -> [Local_CS016]
FEATURE [PartDesign::Pocket] Pocket086
  BaseFeature = -> Pad012
  Direction = (0,0,-1)
  Length = 5
  Length2 = 5
  Midplane = true
  Profile = -> Binder043
  Type = 1
FEATURE [PartDesign::CoordinateSystem] Local_CS044
  AttacherType = Attacher::AttachEngine3D
  AttachmentOffset = pos=(119.5,11.5,0) rot=(0,0,1;0rad)
  MapMode = 5
  Placement = pos=(97.74,69.7093,0) rot=(0,0,1;0.523599rad)
  Support = -> [Local_CS016]
FEATURE [PartDesign::SubShapeBinder] Binder046
  BindCopyOnChange = 0
  BindMode = 0
  ClaimChildren = false
  Context = -> Model [Body001003005002.Binder046.]
  Fuse = false
  MakeFace = true
  OffsetFill = false
  OffsetIntersection = false
  OffsetJoinType = 0
  OffsetOpenResult = false
  PartialLoad = false
  Placement = pos=(97.74,69.7093,0) rot=(0,0,1;0.523599rad)
  Relative = false
  Support = -> [Body001[Pocket073.Sketch073.]]
  _Version = 2
FEATURE [PartDesign::Pocket] Pocket089
  BaseFeature = -> Pocket086
  Direction = (0,0,-1)
  Length = 5
  Length2 = 5
  Midplane = true
  Profile = -> Binder046
  Type = 1
FEATURE [PartDesign::Mirrored] Mirrored014
  BaseFeature = -> Pocket089
  MirrorPlane = -> Sketch047 [V_Axis]
  Originals = -> [Pad012,Pocket086,Pocket089]
  Refine = true
FEATURE [PartDesign::Pocket] Pocket084
  BaseFeature = -> Mirrored014
  Direction = (0,0,-1)
  Length = 5
  Length2 = 5
  Midplane = true
  Profile = -> Binder041
  Type = 1
FEATURE [PartDesign::Pocket] Pocket085
  BaseFeature = -> Pocket084
  Direction = (0,0,-1)
  Length = 5
  Length2 = 5
  Midplane = true
  Profile = -> Binder042
  Type = 1
FEATURE [PartDesign::Body] Body001003005  label="basin_cover"
  Group = -> [Sketch047,Pad012,Pocket086,Pocket089,Mirrored014,Local_CS013,Local_CS016,DatumPlane015,DatumPlane016,Local_CS026,Binder041,Binder042,Pocket084,Pocket085,Binder043,Local_CS043,Local_CS044,Binder046]
  Origin = -> Origin014
  Placement = pos=(0,0,0) rot=(0,0,1;1.0472rad)
  Tip = -> Pocket085
COMPONENT P2 — recipe-attached ("basement", modeled in this document).
Construction recipe (the document's own serialized feature program — sketch geometry with constraints, then the solid features built on it; lengths are millimeters unless a unit is written):

FEATURE [Sketcher::SketchObject] Sketch048
  FullyConstrained = true
  MapMode = 5
  Support = -> [XY_Plane016]
  sketch-geometry (1):
    g0: Circle CenterX=0 CenterY=0 CenterZ=0 NormalX=0 NormalY=0 NormalZ=1 AngleXU=0 Radius=211.375
  constraints (2):
    c: Coincident(g0,g-1)
    c: Radius(g0) = 211.375
FEATURE [PartDesign::Pad] Pad013
  Direction = (0,0,1)
  Length = 3
  Length2 = 10
  Profile = -> Sketch048
  ReferenceAxis = -> Sketch048 [N_Axis]
  Type = 0
FEATURE [Sketcher::SketchObject] Sketch049
  AttachmentOffset = pos=(0,195.697,0) rot=(0,0,1;0rad)
  FullyConstrained = true
  MapMode = 5
  Placement = pos=(0,195.697,0) rot=(0,0,1;0rad)
  Support = -> [XY_Plane016]
  sketch-geometry (9):
    g0: ArcOfCircle CenterX=-11.5 CenterY=8.0875 CenterZ=0 NormalX=0 NormalY=0 NormalZ=1 AngleXU=0 Radius=1.5875 StartAngle=1.5708 EndAngle=4.71239
    g1: LineSegment StartX=-11.5 StartY=6.5 StartZ=0 EndX=8.325 EndY=6.5 EndZ=0
    g2: LineSegment StartX=8.325 StartY=6.5 StartZ=0 EndX=8.325 EndY=0 EndZ=0
    g3: LineSegment StartX=8.325 StartY=0 StartZ=0 EndX=11.5 EndY=0 EndZ=0
    g4: LineSegment StartX=11.5 StartY=0 StartZ=0 EndX=11.5 EndY=6.5 EndZ=0
    g5: LineSegment StartX=-11.5 StartY=9.675 StartZ=0 EndX=8.325 EndY=9.675 EndZ=0
    g6: ArcOfCircle CenterX=8.325 CenterY=6.5 CenterZ=0 NormalX=0 NormalY=0 NormalZ=1 AngleXU=0 Radius=3.175 StartAngle=6e-16 EndAngle=1.5708
    g7: GeomPoint X=8.325 Y=-6.5 Z=0
    g8: GeomPoint X=8.325 Y=-9.675 Z=0
  constraints (21):
    c: Horizontal(g1)
    c: PointOnObject(g2,g-1)
    c: Vertical(g2)
    c: Coincident(g3,g2)
    c: PointOnObject(g3,g-1)
    c: Coincident(g4,g3)
    c: Vertical(g4)
    c: Horizontal(g5)
    c: Tangent(g6,g4) = -1.5708
    c: Tangent(g6,g5) = 1.5708
    c: DistanceX(g3) = 11.5
    c: Tangent(g1,g0) = -1.5708
    c: Tangent(g5,g0) = 1.5708
    c: Diameter(g0) = 3.175
    c: DistanceX(g0) = -11.5
    c: Coincident(g6,g2)
    c: Coincident(g2,g1)
    c: Symmetric(g7,g1,g2)
    c: DistanceY(g7,g1) = 13  'cut_width'
    c: Symmetric(g8,g5,g2)
    c: DistanceY(g8,g5) = 19.35  'total_width'
FEATURE [Sketcher::SketchObject] Sketch050
  AttachmentOffset = pos=(0,195.697,0) rot=(0,0,1;0rad)
  FullyConstrained = true
  MapMode = 5
  Placement = pos=(0,195.697,0) rot=(0,0,1;0rad)
  Support = -> [XY_Plane016]
  sketch-geometry (17):
    g0: LineSegment StartX=-11.5 StartY=-8.0875 StartZ=0 EndX=-11.5 EndY=8.0875 EndZ=0
    g1: ArcOfCircle CenterX=-11.5 CenterY=8.0875 CenterZ=0 NormalX=0 NormalY=0 NormalZ=1 AngleXU=0 Radius=1.5875 StartAngle=1.5708 EndAngle=4.71239
    g2: LineSegment StartX=-11.5 StartY=6.5 StartZ=0 EndX=8.325 EndY=6.5 EndZ=0
    g3: LineSegment StartX=8.325 StartY=6.5 StartZ=0 EndX=8.325 EndY=0 EndZ=0
    g4: LineSegment StartX=8.325 StartY=0 StartZ=0 EndX=11.5 EndY=0 EndZ=0
    g5: LineSegment StartX=11.5 StartY=0 StartZ=0 EndX=11.5 EndY=6.5 EndZ=0
    g6: LineSegment StartX=-11.5 StartY=9.675 StartZ=0 EndX=8.325 EndY=9.675 EndZ=0
    g7: ArcOfCircle CenterX=8.325 CenterY=6.5 CenterZ=0 NormalX=0 NormalY=0 NormalZ=1 AngleXU=0 Radius=3.175 StartAngle=1.83e-14 EndAngle=1.5708
    g8: GeomPoint X=8.325 Y=-6.5 Z=0
    g9: ArcOfCircle CenterX=-11.5 CenterY=11.5875 CenterZ=0 NormalX=0 NormalY=0 NormalZ=1 AngleXU=0 Radius=1.5875 StartAngle=1.5708 EndAngle=4.71239
    g10: LineSegment StartX=-11.5 StartY=10 StartZ=0 EndX=8.325 EndY=10 EndZ=0
    g11: LineSegment StartX=8.325 StartY=10 StartZ=0 EndX=8.325 EndY=0 EndZ=0
    g12: LineSegment StartX=8.325 StartY=0 StartZ=0 EndX=11.5 EndY=0 EndZ=0
    g13: LineSegment StartX=11.5 StartY=0 StartZ=0 EndX=11.5 EndY=10 EndZ=0
    g14: LineSegment StartX=-11.5 StartY=13.175 StartZ=0 EndX=8.325 EndY=13.175 EndZ=0
    g15: ArcOfCircle CenterX=8.325 CenterY=10 CenterZ=0 NormalX=0 NormalY=0 NormalZ=1 AngleXU=0 Radius=3.175 StartAngle=1.5915e-12 EndAngle=1.5708
    g16: GeomPoint X=8.325 Y=-10 Z=0
  constraints (40):
    c: Horizontal(g2)
    c: PointOnObject(g3,g-1)
    c: Vertical(g3)
    c: Coincident(g4,g3)
    c: PointOnObject(g4,g-1)
    c: Coincident(g5,g4)
    c: Vertical(g5)
    c: Horizontal(g6)
    c: Tangent(g7,g5) = -1.5708
    c: Tangent(g7,g6) = 1.5708
    c: DistanceX(g4) = 11.5
    c: Tangent(g2,g1) = -1.5708
    c: Tangent(g6,g1) = 1.5708
    c: Diameter(g1) = 3.175
    c: DistanceX(g1) = -11.5
    c: Coincident(g7,g3)
    c: Coincident(g3,g2)
    c: Symmetric(g8,g2,g3)
    c: DistanceY(g8,g2) = 13  'cut_width'
    c: Horizontal(g10)
    c: PointOnObject(g11,g-1)
    c: Vertical(g11)
    c: Coincident(g12,g11)
    c: PointOnObject(g12,g-1)
    c: Coincident(g13,g12)
    c: Vertical(g13)
    c: Horizontal(g14)
    c: Tangent(g15,g13) = -1.5708
    c: Tangent(g15,g14) = 1.5708
    c: DistanceX(g12) = 11.5
    c: Tangent(g10,g9) = -1.5708
    c: Tangent(g14,g9) = 1.5708
    c: Diameter(g9) = 3.175
    c: DistanceX(g9) = -11.5
    c: Coincident(g15,g11)
    c: Coincident(g11,g10)
    c: Symmetric(g16,g10,g11)
    c: DistanceY(g16,g10) = 20  'cut_width'
    c: Coincident(g0,g1)
    c: Symmetric(g0,g0,g-1)
FEATURE [PartDesign::CoordinateSystem] Local_CS017
  AttacherType = Attacher::AttachEngine3D
  AttachmentOffset = pos=(0,0,3) rot=(0,0,1;0rad)
  MapMode = 5
  Placement = pos=(0,0,3) rot=(0,0,1;0rad)
  Support = -> [XY_Plane016]
FEATURE [PartDesign::SubShapeBinder] Binder004
  AttacherType = Attacher::AttachEngine3D
  AttachmentOffset = pos=(0,195.697,0) rot=(0,0,1;3.14159rad)
  BindCopyOnChange = 0
  BindMode = 0
  ClaimChildren = false
  Context = -> Model [Body001003005003002.Binder004.]
  Fuse = false
  MakeFace = true
  MapMode = 5
  OffsetFill = false
  OffsetIntersection = false
  OffsetJoinType = 0
  OffsetOpenResult = false
  PartialLoad = false
  Placement = pos=(0,179.522,0) rot=(0,0,1;3.14159rad)
  Relative = false
  _Version = 2
FEATURE [PartDesign::Plane] DatumPlane017
  Length = 60
  MapMode = 3
  Placement = pos=(0,179.522,0) rot=(0,0.707107,0.707107;3.14159rad)
  ResizeMode = 0
  Support = -> [Binder004]
  Width = 60
FEATURE [Sketcher::SketchObject] Sketch051
  AttachmentOffset = pos=(0,179.522,0) rot=(0,0,1;0rad)
  FullyConstrained = true
  MapMode = 5
  Placement = pos=(0,179.522,0) rot=(0,0,1;0rad)
  Support = -> [XY_Plane016]
  sketch-geometry (9):
    g0: ArcOfCircle CenterX=-11.5 CenterY=8.0875 CenterZ=0 NormalX=0 NormalY=0 NormalZ=1 AngleXU=0 Radius=1.5875 StartAngle=1.5708 EndAngle=4.71239
    g1: LineSegment StartX=-11.5 StartY=6.5 StartZ=0 EndX=8.325 EndY=6.5 EndZ=0
    g2: LineSegment StartX=8.325 StartY=6.5 StartZ=0 EndX=8.325 EndY=0 EndZ=0
    g3: LineSegment StartX=8.325 StartY=0 StartZ=0 EndX=11.5 EndY=0 EndZ=0
    g4: LineSegment StartX=11.5 StartY=0 StartZ=0 EndX=11.5 EndY=6.5 EndZ=0
    g5: LineSegment StartX=-11.5 StartY=9.675 StartZ=0 EndX=8.325 EndY=9.675 EndZ=0
    g6: ArcOfCircle CenterX=8.325 CenterY=6.5 CenterZ=0 NormalX=0 NormalY=0 NormalZ=1 AngleXU=0 Radius=3.175 StartAngle=0 EndAngle=1.5708
    g7: GeomPoint X=8.325 Y=-6.5 Z=0
    g8: LineSegment StartX=11.5 StartY=8.0875 StartZ=0 EndX=11.5 EndY=-8.0875 EndZ=0
  constraints (22):
    c: Horizontal(g1)
    c: PointOnObject(g2,g-1)
    c: Vertical(g2)
    c: Coincident(g3,g2)
    c: PointOnObject(g3,g-1)
    c: Coincident(g4,g3)
    c: Vertical(g4)
    c: Horizontal(g5)
    c: Tangent(g6,g4) = -1.5708
    c: Tangent(g6,g5) = 1.5708
    c: DistanceX(g3) = 11.5
    c: Tangent(g1,g0) = -1.5708
    c: Tangent(g5,g0) = 1.5708
    c: Diameter(g0) = 3.175
    c: DistanceX(g0) = -11.5
    c: Coincident(g6,g2)
    c: Coincident(g2,g1)
    c: Symmetric(g7,g1,g2)
    c: DistanceY(g7,g1) = 13  'cut_width'
    c: Vertical(g8)
    c: Symmetric(g0,g8,g-1)
    c: Horizontal(g8,g0)
FEATURE [PartDesign::SubShapeBinder] Binder005
  AttacherType = Attacher::AttachEngine3D
  AttachmentOffset = pos=(0,0,0) rot=(0,0,1;1.0472rad)
  BindCopyOnChange = 0
  BindMode = 0
  ClaimChildren = false
  Context = -> Body001003005003 [Binder005.]
  Fuse = false
  MakeFace = true
  MapMode = 5
  OffsetFill = false
  OffsetIntersection = false
  OffsetJoinType = 0
  OffsetOpenResult = false
  PartialLoad = false
  Placement = pos=(0,0,0) rot=(0,0,1;1.0472rad)
  Relative = false
  _Version = 2
FEATURE [PartDesign::Plane] DatumPlane018
  Length = 79.989
  MapMode = 4
  Placement = pos=(0,0,0) rot=(0.186157,0.694747,0.694747;2.77349rad)
  ResizeMode = 0
  Support = -> [Binder005]
  Width = 61.6877
FEATURE [Sketcher::SketchObject] Sketch057
  AttachmentOffset = pos=(195.697,-11.5,0) rot=(0,0,1;0rad)
  FullyConstrained = true
  MapMode = 5
  Placement = pos=(4.6e-14,195.697,-11.5) rot=(0.57735,0.57735,0.57735;2.0944rad)
  Support = -> [YZ_Plane015]
  sketch-geometry (1):
    g0: Circle CenterX=0 CenterY=0 CenterZ=0 NormalX=0 NormalY=0 NormalZ=1 AngleXU=0 Radius=1.7
  constraints (2):
    c: Coincident(g0,g-1)
    c: Diameter(g0) = 3.4
FEATURE [Sketcher::SketchObject] Sketch058
  AttachmentOffset = pos=(179.522,-11.5,0) rot=(0,0,1;0rad)
  FullyConstrained = true
  MapMode = 5
  Placement = pos=(4.24e-14,179.522,-11.5) rot=(0.57735,0.57735,0.57735;2.0944rad)
  Support = -> [YZ_Plane015]
  sketch-geometry (1):
    g0: Circle CenterX=0 CenterY=0 CenterZ=0 NormalX=0 NormalY=0 NormalZ=1 AngleXU=0 Radius=1.7
  constraints (2):
    c: Coincident(g0,g-1)
    c: Diameter(g0) = 3.4
FEATURE [PartDesign::Pocket] Pocket027
  BaseFeature = -> Pad013
  Direction = (-1,2e-16,-3e-16)
  Length = 5
  Length2 = 5
  Midplane = true
  Profile = -> Sketch058
  ReferenceAxis = -> Sketch058 [N_Axis]
  Type = 1
FEATURE [PartDesign::CoordinateSystem] Local_CS021
  AttacherType = Attacher::AttachEngine3D
  AttachmentOffset = pos=(0,0,0) rot=(0,0,1;2.0944rad)
  MapMode = 5
  Placement = pos=(0,0,0) rot=(0,0,1;2.0944rad)
  Support = -> [XY_Plane016]
FEATURE [PartDesign::CoordinateSystem] Local_CS022
  AttacherType = Attacher::AttachEngine3D
  AttachmentOffset = pos=(0,0,0) rot=(0,0,-1;2.0944rad)
  MapMode = 5
  Placement = pos=(0,0,0) rot=(0,0,-1;2.0944rad)
  Support = -> [XY_Plane016]
FEATURE [PartDesign::Plane] DatumPlane019
  Length = 81.9615
  MapMode = 5
  Placement = pos=(0,0,0) rot=(0,0,1;2.0944rad)
  ResizeMode = 0
  Support = -> [Local_CS021]
  Width = 81.9615
FEATURE [PartDesign::Plane] DatumPlane020
  Length = 81.9615
  MapMode = 5
  Placement = pos=(0,0,0) rot=(0,0,-1;2.0944rad)
  ResizeMode = 0
  Support = -> [Local_CS022]
  Width = 81.9615
FEATURE [Sketcher::SketchObject] Sketch061
  AttachmentOffset = pos=(0,195.697,0) rot=(0,0,1;0rad)
  FullyConstrained = true
  MapMode = 5
  Placement = pos=(-169.478,-97.8483,0) rot=(0,0,1;2.0944rad)
  Support = -> [DatumPlane019]
  sketch-geometry (17):
    g0: LineSegment StartX=-11.5 StartY=-8.0875 StartZ=0 EndX=-11.5 EndY=8.0875 EndZ=0
    g1: ArcOfCircle CenterX=-11.5 CenterY=8.0875 CenterZ=0 NormalX=0 NormalY=0 NormalZ=1 AngleXU=0 Radius=1.5875 StartAngle=1.5708 EndAngle=4.71239
    g2: LineSegment StartX=-11.5 StartY=6.5 StartZ=0 EndX=8.325 EndY=6.5 EndZ=0
    g3: LineSegment StartX=8.325 StartY=6.5 StartZ=0 EndX=8.325 EndY=0 EndZ=0
    g4: LineSegment StartX=8.325 StartY=0 StartZ=0 EndX=11.5 EndY=0 EndZ=0
    g5: LineSegment StartX=11.5 StartY=0 StartZ=0 EndX=11.5 EndY=6.5 EndZ=0
    g6: LineSegment StartX=-11.5 StartY=9.675 StartZ=0 EndX=8.325 EndY=9.675 EndZ=0
    g7: ArcOfCircle CenterX=8.325 CenterY=6.5 CenterZ=0 NormalX=0 NormalY=0 NormalZ=1 AngleXU=0 Radius=3.175 StartAngle=0 EndAngle=1.5708
    g8: GeomPoint X=8.325 Y=-6.5 Z=0
    g9: ArcOfCircle CenterX=-11.5 CenterY=11.5875 CenterZ=0 NormalX=0 NormalY=0 NormalZ=1 AngleXU=0 Radius=1.5875 StartAngle=1.5708 EndAngle=4.71239
    g10: LineSegment StartX=-11.5 StartY=10 StartZ=0 EndX=8.325 EndY=10 EndZ=0
    g11: LineSegment StartX=8.325 StartY=10 StartZ=0 EndX=8.325 EndY=0 EndZ=0
    g12: LineSegment StartX=8.325 StartY=0 StartZ=0 EndX=11.5 EndY=0 EndZ=0
    g13: LineSegment StartX=11.5 StartY=0 StartZ=0 EndX=11.5 EndY=10 EndZ=0
    g14: LineSegment StartX=-11.5 StartY=13.175 StartZ=0 EndX=8.325 EndY=13.175 EndZ=0
    g15: ArcOfCircle CenterX=8.325 CenterY=10 CenterZ=0 NormalX=0 NormalY=0 NormalZ=1 AngleXU=0 Radius=3.175 StartAngle=1.5915e-12 EndAngle=1.5708
    g16: GeomPoint X=8.325 Y=-10 Z=0
  constraints (40):
    c: Horizontal(g2)
    c: PointOnObject(g3,g-1)
    c: Vertical(g3)
    c: Coincident(g4,g3)
    c: PointOnObject(g4,g-1)
    c: Coincident(g5,g4)
    c: Vertical(g5)
    c: Horizontal(g6)
    c: Tangent(g7,g5) = -1.5708
    c: Tangent(g7,g6) = 1.5708
    c: DistanceX(g4) = 11.5
    c: Tangent(g2,g1) = -1.5708
    c: Tangent(g6,g1) = 1.5708
    c: Diameter(g1) = 3.175
    c: DistanceX(g1) = -11.5
    c: Coincident(g7,g3)
    c: Coincident(g3,g2)
    c: Symmetric(g8,g2,g3)
    c: DistanceY(g8,g2) = 13  'cut_width'
    c: Horizontal(g10)
    c: PointOnObject(g11,g-1)
    c: Vertical(g11)
    c: Coincident(g12,g11)
    c: PointOnObject(g12,g-1)
    c: Coincident(g13,g12)
    c: Vertical(g13)
    c: Horizontal(g14)
    c: Tangent(g15,g13) = -1.5708
    c: Tangent(g15,g14) = 1.5708
    c: DistanceX(g12) = 11.5
    c: Tangent(g10,g9) = -1.5708
    c: Tangent(g14,g9) = 1.5708
    c: Diameter(g9) = 3.175
    c: DistanceX(g9) = -11.5
    c: Coincident(g15,g11)
    c: Coincident(g11,g10)
    c: Symmetric(g16,g10,g11)
    c: DistanceY(g16,g10) = 20  'cut_width'
    c: Coincident(g0,g1)
    c: Symmetric(g0,g0,g-1)
FEATURE [Sketcher::SketchObject] Sketch062
  AttachmentOffset = pos=(0,195.697,0) rot=(0,0,1;0rad)
  FullyConstrained = true
  MapMode = 5
  Placement = pos=(169.478,-97.8483,0) rot=(0,0,-1;2.0944rad)
  Support = -> [DatumPlane020]
  sketch-geometry (17):
    g0: LineSegment StartX=-11.5 StartY=-8.0875 StartZ=0 EndX=-11.5 EndY=8.0875 EndZ=0
    g1: ArcOfCircle CenterX=-11.5 CenterY=8.0875 CenterZ=0 NormalX=0 NormalY=0 NormalZ=1 AngleXU=0 Radius=1.5875 StartAngle=1.5708 EndAngle=4.71239
    g2: LineSegment StartX=-11.5 StartY=6.5 StartZ=0 EndX=8.325 EndY=6.5 EndZ=0
    g3: LineSegment StartX=8.325 StartY=6.5 StartZ=0 EndX=8.325 EndY=0 EndZ=0
    g4: LineSegment StartX=8.325 StartY=0 StartZ=0 EndX=11.5 EndY=0 EndZ=0
    g5: LineSegment StartX=11.5 StartY=0 StartZ=0 EndX=11.5 EndY=6.5 EndZ=0
    g6: LineSegment StartX=-11.5 StartY=9.675 StartZ=0 EndX=8.325 EndY=9.675 EndZ=0
    g7: ArcOfCircle CenterX=8.325 CenterY=6.5 CenterZ=0 NormalX=0 NormalY=0 NormalZ=1 AngleXU=0 Radius=3.175 StartAngle=0 EndAngle=1.5708
    g8: GeomPoint X=8.325 Y=-6.5 Z=0
    g9: ArcOfCircle CenterX=-11.5 CenterY=11.5875 CenterZ=0 NormalX=0 NormalY=0 NormalZ=1 AngleXU=0 Radius=1.5875 StartAngle=1.5708 EndAngle=4.71239
    g10: LineSegment StartX=-11.5 StartY=10 StartZ=0 EndX=8.325 EndY=10 EndZ=0
    g11: LineSegment StartX=8.325 StartY=10 StartZ=0 EndX=8.325 EndY=0 EndZ=0
    g12: LineSegment StartX=8.325 StartY=0 StartZ=0 EndX=11.5 EndY=0 EndZ=0
    g13: LineSegment StartX=11.5 StartY=0 StartZ=0 EndX=11.5 EndY=10 EndZ=0
    g14: LineSegment StartX=-11.5 StartY=13.175 StartZ=0 EndX=8.325 EndY=13.175 EndZ=0
    g15: ArcOfCircle CenterX=8.325 CenterY=10 CenterZ=0 NormalX=0 NormalY=0 NormalZ=1 AngleXU=0 Radius=3.175 StartAngle=1.5915e-12 EndAngle=1.5708
    g16: GeomPoint X=8.325 Y=-10 Z=0
  constraints (40):
    c: Horizontal(g2)
    c: PointOnObject(g3,g-1)
    c: Vertical(g3)
    c: Coincident(g4,g3)
    c: PointOnObject(g4,g-1)
    c: Coincident(g5,g4)
    c: Vertical(g5)
    c: Horizontal(g6)
    c: Tangent(g7,g5) = -1.5708
    c: Tangent(g7,g6) = 1.5708
    c: DistanceX(g4) = 11.5
    c: Tangent(g2,g1) = -1.5708
    c: Tangent(g6,g1) = 1.5708
    c: Diameter(g1) = 3.175
    c: DistanceX(g1) = -11.5
    c: Coincident(g7,g3)
    c: Coincident(g3,g2)
    c: Symmetric(g8,g2,g3)
    c: DistanceY(g8,g2) = 13  'cut_width'
    c: Horizontal(g10)
    c: PointOnObject(g11,g-1)
    c: Vertical(g11)
    c: Coincident(g12,g11)
    c: PointOnObject(g12,g-1)
    c: Coincident(g13,g12)
    c: Vertical(g13)
    c: Horizontal(g14)
    c: Tangent(g15,g13) = -1.5708
    c: Tangent(g15,g14) = 1.5708
    c: DistanceX(g12) = 11.5
    c: Tangent(g10,g9) = -1.5708
    c: Tangent(g14,g9) = 1.5708
    c: Diameter(g9) = 3.175
    c: DistanceX(g9) = -11.5
    c: Coincident(g15,g11)
    c: Coincident(g11,g10)
    c: Symmetric(g16,g10,g11)
    c: DistanceY(g16,g10) = 20  'cut_width'
    c: Coincident(g0,g1)
    c: Symmetric(g0,g0,g-1)
FEATURE [Sketcher::SketchObject] Sketch063
  AttachmentOffset = pos=(0,179.522,0) rot=(0,0,1;0rad)
  FullyConstrained = true
  MapMode = 5
  Placement = pos=(-155.47,-89.7608,0) rot=(0,0,1;2.0944rad)
  Support = -> [DatumPlane019]
  sketch-geometry (9):
    g0: ArcOfCircle CenterX=-11.5 CenterY=8.0875 CenterZ=0 NormalX=0 NormalY=0 NormalZ=1 AngleXU=0 Radius=1.5875 StartAngle=1.5708 EndAngle=4.71239
    g1: LineSegment StartX=-11.5 StartY=6.5 StartZ=0 EndX=8.325 EndY=6.5 EndZ=0
    g2: LineSegment StartX=8.325 StartY=6.5 StartZ=0 EndX=8.325 EndY=0 EndZ=0
    g3: LineSegment StartX=8.325 StartY=0 StartZ=0 EndX=11.5 EndY=0 EndZ=0
    g4: LineSegment StartX=11.5 StartY=0 StartZ=0 EndX=11.5 EndY=6.5 EndZ=0
    g5: LineSegment StartX=-11.5 StartY=9.675 StartZ=0 EndX=8.325 EndY=9.675 EndZ=0
    g6: ArcOfCircle CenterX=8.325 CenterY=6.5 CenterZ=0 NormalX=0 NormalY=0 NormalZ=1 AngleXU=0 Radius=3.175 StartAngle=0 EndAngle=1.5708
    g7: GeomPoint X=8.325 Y=-6.5 Z=0
    g8: LineSegment StartX=11.5 StartY=8.0875 StartZ=0 EndX=11.5 EndY=-8.0875 EndZ=0
  constraints (22):
    c: Horizontal(g1)
    c: PointOnObject(g2,g-1)
    c: Vertical(g2)
    c: Coincident(g3,g2)
    c: PointOnObject(g3,g-1)
    c: Coincident(g4,g3)
    c: Vertical(g4)
    c: Horizontal(g5)
    c: Tangent(g6,g4) = -1.5708
    c: Tangent(g6,g5) = 1.5708
    c: DistanceX(g3) = 11.5
    c: Tangent(g1,g0) = -1.5708
    c: Tangent(g5,g0) = 1.5708
    c: Diameter(g0) = 3.175
    c: DistanceX(g0) = -11.5
    c: Coincident(g6,g2)
    c: Coincident(g2,g1)
    c: Symmetric(g7,g1,g2)
    c: DistanceY(g7,g1) = 13  'cut_width'
    c: Vertical(g8)
    c: Symmetric(g0,g8,g-1)
    c: Horizontal(g8,g0)
FEATURE [Sketcher::SketchObject] Sketch064
  AttachmentOffset = pos=(0,179.522,0) rot=(0,0,1;0rad)
  FullyConstrained = true
  MapMode = 5
  Placement = pos=(155.47,-89.7608,0) rot=(0,0,-1;2.0944rad)
  Support = -> [DatumPlane020]
  sketch-geometry (9):
    g0: ArcOfCircle CenterX=-11.5 CenterY=8.0875 CenterZ=0 NormalX=0 NormalY=0 NormalZ=1 AngleXU=0 Radius=1.5875 StartAngle=1.5708 EndAngle=4.71239
    g1: LineSegment StartX=-11.5 StartY=6.5 StartZ=0 EndX=8.325 EndY=6.5 EndZ=0
    g2: LineSegment StartX=8.325 StartY=6.5 StartZ=0 EndX=8.325 EndY=0 EndZ=0
    g3: LineSegment StartX=8.325 StartY=0 StartZ=0 EndX=11.5 EndY=0 EndZ=0
    g4: LineSegment StartX=11.5 StartY=0 StartZ=0 EndX=11.5 EndY=6.5 EndZ=0
    g5: LineSegment StartX=-11.5 StartY=9.675 StartZ=0 EndX=8.325 EndY=9.675 EndZ=0
    g6: ArcOfCircle CenterX=8.325 CenterY=6.5 CenterZ=0 NormalX=0 NormalY=0 NormalZ=1 AngleXU=0 Radius=3.175 StartAngle=0 EndAngle=1.5708
    g7: GeomPoint X=8.325 Y=-6.5 Z=0
    g8: LineSegment StartX=11.5 StartY=8.0875 StartZ=0 EndX=11.5 EndY=-8.0875 EndZ=0
  constraints (22):
    c: Horizontal(g1)
    c: PointOnObject(g2,g-1)
    c: Vertical(g2)
    c: Coincident(g3,g2)
    c: PointOnObject(g3,g-1)
    c: Coincident(g4,g3)
    c: Vertical(g4)
    c: Horizontal(g5)
    c: Tangent(g6,g4) = -1.5708
    c: Tangent(g6,g5) = 1.5708
    c: DistanceX(g3) = 11.5
    c: Tangent(g1,g0) = -1.5708
    c: Tangent(g5,g0) = 1.5708
    c: Diameter(g0) = 3.175
    c: DistanceX(g0) = -11.5
    c: Coincident(g6,g2)
    c: Coincident(g2,g1)
    c: Symmetric(g7,g1,g2)
    c: DistanceY(g7,g1) = 13  'cut_width'
    c: Vertical(g8)
    c: Symmetric(g0,g8,g-1)
    c: Horizontal(g8,g0)
FEATURE [Sketcher::SketchObject] Sketch075
  AttachmentOffset = pos=(0,0,0) rot=(0,0,1;3.14159rad)
  FullyConstrained = true
  MapMode = 5
  Placement = pos=(0,0,0) rot=(0,0,1;3.14159rad)
  Support = -> [XY_Plane016]
  sketch-geometry (6):
    g0: Circle CenterX=64.8152 CenterY=64.8152 CenterZ=0 NormalX=0 NormalY=0 NormalZ=1 AngleXU=0 Radius=1.7
    g1: Circle CenterX=64.8152 CenterY=-64.8152 CenterZ=0 NormalX=0 NormalY=0 NormalZ=1 AngleXU=0 Radius=1.7
    g2: Circle CenterX=-64.8152 CenterY=-64.8152 CenterZ=0 NormalX=0 NormalY=0 NormalZ=1 AngleXU=0 Radius=1.7
    g3: Circle CenterX=-64.8152 CenterY=64.8152 CenterZ=0 NormalX=0 NormalY=0 NormalZ=1 AngleXU=0 Radius=1.7
    g4: LineSegment StartX=-64.8152 StartY=64.8152 StartZ=0 EndX=64.8152 EndY=64.8152 EndZ=0
    g5: LineSegment StartX=64.8152 StartY=64.8152 StartZ=0 EndX=64.8152 EndY=-64.8152 EndZ=0
  constraints (13):
    c: Symmetric(g3,g0,g-2)
    c: Symmetric(g0,g1,g-1)
    c: Symmetric(g0,g2,g-1)
    c: Equal(g0,g3)
    c: Equal(g0,g2)
    c: Equal(g0,g1)
    c: Diameter(g0) = 3.4
    c: Coincident(g4,g3)
    c: Coincident(g4,g0)
    c: Coincident(g5,g0)
    c: Coincident(g5,g1)
    c: Equal(g5,g4)
    c: Distance(g2,g0) = 183.325
FEATURE [PartDesign::Pocket] Pocket036
  BaseFeature = -> Pocket027
  Direction = (0,0,-1)
  Length = 5
  Length2 = 5
  Midplane = true
  Profile = -> Sketch075
  ReferenceAxis = -> Sketch075 [N_Axis]
  Type = 1
FEATURE [PartDesign::SubShapeBinder] Binder018
  BindCopyOnChange = 0
  BindMode = 0
  ClaimChildren = true
  Context = -> Body001003005003 [Binder018.]
  Fuse = false
  MakeFace = true
  OffsetFill = false
  OffsetIntersection = false
  OffsetJoinType = 0
  OffsetOpenResult = false
  PartialLoad = false
  Relative = false
  Support = -> [Body001003005003012[Pocket039.Sketch080.]]
  _Version = 2
FEATURE [PartDesign::SubShapeBinder] Binder023
  BindCopyOnChange = 0
  BindMode = 0
  ClaimChildren = false
  Context = -> Body001003005003 [Binder023.]
  Fuse = false
  MakeFace = true
  OffsetFill = false
  OffsetIntersection = false
  OffsetJoinType = 0
  OffsetOpenResult = false
  PartialLoad = false
  Relative = true
  Support = -> [Body001003005003013[Pocket042.Sketch084.,Pocket041.Sketch083.]]
  _Version = 2
FEATURE [PartDesign::SubShapeBinder] Binder036
  BindCopyOnChange = 0
  BindMode = 0
  ClaimChildren = false
  Context = -> Body001003005003 [Binder036.]
  Fuse = false
  MakeFace = true
  OffsetFill = false
  OffsetIntersection = false
  OffsetJoinType = 0
  OffsetOpenResult = false
  PartialLoad = false
  Placement = pos=(11.5,180,0) rot=(0,0,1;1.5708rad)
  Relative = true
  Support = -> [Body_7[Pocket061.Sketch105.]]
  _Version = 2
FEATURE [PartDesign::Pocket] Pocket074
  BaseFeature = -> Pocket036
  Direction = (0,0,-1)
  Length = 5
  Length2 = 5
  Midplane = true
  Profile = -> Binder036
  Type = 1
FEATURE [PartDesign::Mirrored] Mirrored
  MirrorPlane = -> YZ_Plane015
FEATURE [PartDesign::PolarPattern] PolarPattern015
  Angle = 360
  Axis = -> Z_Axis015
  Occurrences = 3
FEATURE [PartDesign::MultiTransform] MultiTransform
  BaseFeature = -> Pocket074
  Originals = -> [Pocket074]
  Transformations = -> [Mirrored,PolarPattern015]
FEATURE [Sketcher::SketchObject] Sketch120
  AttachmentOffset = pos=(0,-70,0) rot=(0,0,1;0rad)
  FullyConstrained = true
  MapMode = 5
  Placement = pos=(0,-70,0) rot=(0,0,1;0rad)
  Support = -> [XY_Plane016]
  sketch-geometry (1):
    g0: Circle CenterX=0 CenterY=0 CenterZ=0 NormalX=0 NormalY=0 NormalZ=1 AngleXU=0 Radius=4.25
  constraints (2):
    c: Coincident(g0,g-1)
    c: Diameter(g0) = 8.5
FEATURE [PartDesign::Pocket] Pocket087
  BaseFeature = -> MultiTransform
  Direction = (0,0,-1)
  Length = 5
  Length2 = 5
  Midplane = true
  Profile = -> Binder023
  Type = 1
FEATURE [PartDesign::PolarPattern] PolarPattern018
  Angle = 120
  Axis = -> Z_Axis015
  BaseFeature = -> Pocket087
  Occurrences = 2
  Originals = -> [Pocket087]
FEATURE [Sketcher::SketchObject] Sketch132
  FullyConstrained = true
  MapMode = 5
  Support = -> [XY_Plane016]
  sketch-geometry (3):
    g0: Circle CenterX=0 CenterY=0 CenterZ=0 NormalX=0 NormalY=0 NormalZ=1 AngleXU=0 Radius=211.375
    g1: Circle CenterX=0 CenterY=0 CenterZ=0 NormalX=0 NormalY=0 NormalZ=1 AngleXU=0 Radius=201.375
    g2: LineSegment StartX=201.375 StartY=0 StartZ=0 EndX=211.375 EndY=0 EndZ=0
  constraints (8):
    c: Coincident(g0,g-1)
    c: Radius(g0) = 211.375
    c: Coincident(g1,g0)
    c: PointOnObject(g2,g1)
    c: PointOnObject(g2,g0)
    c: Horizontal(g2)
    c: PointOnObject(g0,g2)
    c: DistanceX(g2,g2) = 10
FEATURE [PartDesign::Pad] Pad030
  BaseFeature = -> PolarPattern018
  Direction = (0,0,1)
  Length = 3
  Length2 = 10
  Profile = -> Sketch132
  ReferenceAxis = -> Sketch132 [N_Axis]
  Type = 0
FEATURE [PartDesign::Body] Body001003005003  label="basement"
  Group = -> [Sketch048,Pad013,Sketch049,Binder004,DatumPlane017,Sketch050,Local_CS017,Sketch051,Binder005,DatumPlane018,Sketch057,Sketch058,Pocket027,Local_CS021,Local_CS022,DatumPlane019,DatumPlane020,Sketch061,Sketch062,Sketch063,Sketch064,Sketch075,Pocket036,Binder018,Binder023,Binder036,Pocket074,MultiTransform,Mirrored,PolarPattern015,Sketch120,Pocket087,PolarPattern018,Sketch132,Pad030]
  Origin = -> Origin015
  Tip = -> Pad030
COMPONENT P3 — recipe-attached ("Body001003005003003", modeled in this document).
Construction recipe (the document's own serialized feature program — sketch geometry with constraints, then the solid features built on it; lengths are millimeters unless a unit is written):

FEATURE [Sketcher::SketchObject] Sketch052
  FullyConstrained = true
  MapMode = 5
  Support = -> [XY_Plane017]
  sketch-geometry (6):
    g0: ArcOfCircle CenterX=0 CenterY=0 CenterZ=0 NormalX=0 NormalY=0 NormalZ=1 AngleXU=0 Radius=198.875 StartAngle=0.69333 EndAngle=1.5708
    g1: ArcOfCircle CenterX=0 CenterY=0 CenterZ=0 NormalX=0 NormalY=0 NormalZ=1 AngleXU=0 Radius=208.875 StartAngle=0.69333 EndAngle=1.5708
    g2: ArcOfCircle CenterX=156.805 CenterY=130.297 CenterZ=0 NormalX=0 NormalY=0 NormalZ=1 AngleXU=0 Radius=5 StartAngle=3.83492 EndAngle=6.97652
    g3: LineSegment StartX=1.22e-14 StartY=198.875 StartZ=0 EndX=1.28e-14 EndY=208.875 EndZ=0
    g4: ArcOfCircle CenterX=0 CenterY=0 CenterZ=0 NormalX=0 NormalY=0 NormalZ=1 AngleXU=0 Radius=203.875 StartAngle=0.668805 EndAngle=1.5708
    g5: LineSegment StartX=0 StartY=0 StartZ=0 EndX=176.561 EndY=101.938 EndZ=0
  constraints (18):
    c: Coincident(g0,g-1)
    c: PointOnObject(g0,g-2)
    c: Coincident(g1,g0)
    c: PointOnObject(g1,g-2)
    c: Coincident(g3,g1)
    c: DistanceY(g1) = 208.875  'r'
    c: DistanceY(g0,g1) = 10  'width'
    c: Tangent(g2,g0) = 1.5708
    c: Tangent(g2,g1) = -1.5708
    c: Coincident(g4,g0)
    c: PointOnObject(g4,g2)
    c: Coincident(g5,g0)
    c: Angle(g-1,g5) = 0.523599
    c: Distance(g4,g5) = 29.5
    c: Coincident(g3,g0)
    c: PointOnObject(g2,g4)
    c: PointOnObject(g4,g-2)
    c: PointOnObject(g5,g4)
FEATURE [PartDesign::Pad] Pad014
  Direction = (0,0,1)
  Length = 3
  Length2 = 10
  Profile = -> Sketch052
  ReferenceAxis = -> Sketch052 [N_Axis]
  Type = 0
FEATURE [PartDesign::CoordinateSystem] Local_CS018
  AttacherType = Attacher::AttachEngine3D
  MapMode = 5
  Support = -> [XY_Plane017]
FEATURE [Sketcher::SketchObject] Sketch055
  FullyConstrained = true
  MapMode = 5
  Support = -> [XY_Plane017]
  sketch-geometry (9):
    g0: ArcOfCircle CenterX=0 CenterY=0 CenterZ=0 NormalX=0 NormalY=0 NormalZ=1 AngleXU=0 Radius=198.875 StartAngle=0.69333 EndAngle=1.5708
    g1: ArcOfCircle CenterX=0 CenterY=0 CenterZ=0 NormalX=0 NormalY=0 NormalZ=1 AngleXU=0 Radius=208.875 StartAngle=0.69333 EndAngle=1.5708
    g2: ArcOfCircle CenterX=156.805 CenterY=130.297 CenterZ=0 NormalX=0 NormalY=0 NormalZ=1 AngleXU=0 Radius=5 StartAngle=3.83492 EndAngle=6.97652
    g3: LineSegment StartX=1.22e-14 StartY=198.875 StartZ=0 EndX=1.28e-14 EndY=208.875 EndZ=0
    g4: ArcOfCircle CenterX=0 CenterY=0 CenterZ=0 NormalX=0 NormalY=0 NormalZ=1 AngleXU=0 Radius=203.875 StartAngle=0.668805 EndAngle=1.5708
    g5: LineSegment StartX=0 StartY=0 StartZ=0 EndX=176.561 EndY=101.938 EndZ=0
    g6: LineSegment StartX=1.22e-14 StartY=202.175 StartZ=0 EndX=1.3e-14 EndY=205.575 EndZ=0
    g7: ArcOfCircle CenterX=1.25e-14 CenterY=203.875 CenterZ=0 NormalX=0 NormalY=0 NormalZ=1 AngleXU=0 Radius=1.7 StartAngle=4.71239 EndAngle=7.85398
    g8: Circle CenterX=143.11 CenterY=145.206 CenterZ=0 NormalX=0 NormalY=0 NormalZ=1 AngleXU=0 Radius=1.7
  constraints (27):
    c: Coincident(g0,g-1)
    c: PointOnObject(g0,g-2)
    c: Coincident(g1,g0)
    c: PointOnObject(g1,g-2)
    c: Coincident(g3,g1)
    c: DistanceY(g1) = 208.875  'r'
    c: DistanceY(g0,g1) = 10  'width'
    c: Tangent(g2,g0) = 1.5708
    c: Tangent(g2,g1) = -1.5708
    c: Coincident(g4,g0)
    c: PointOnObject(g4,g2)
    c: Coincident(g5,g0)
    c: Angle(g-1,g5) = 0.523599
    c: Distance(g4,g5) = 29.5
    c: Coincident(g3,g0)
    c: PointOnObject(g2,g4)
    c: PointOnObject(g4,g-2)
    c: PointOnObject(g5,g4)
    c: PointOnObject(g6,g3)
    c: PointOnObject(g6,g3)
    c: Coincident(g7,g4)
    c: Coincident(g7,g6)
    c: Coincident(g7,g6)
    c: PointOnObject(g8,g4)
    c: Equal(g8,g7)
    c: Diameter(g7) = 3.4
    c: DistanceX(g8) = 143.11
FEATURE [PartDesign::Pocket] Pocket019
  BaseFeature = -> Pad014
  Direction = (0,0,-1)
  Length = 5
  Length2 = 5
  Midplane = true
  Profile = -> Sketch055
  ReferenceAxis = -> Sketch055 [N_Axis]
  Type = 1
FEATURE [PartDesign::Mirrored] Mirrored019
  BaseFeature = -> Pocket019
  MirrorPlane = -> Sketch052 [V_Axis]
  Originals = -> [Pad014,Pocket019]
FEATURE [PartDesign::Body] Body001003005003003
  Group = -> [Sketch052,Pad014,Pocket019,Mirrored019,Local_CS018,Sketch055]
  Origin = -> Origin016
  Tip = -> Mirrored019
COMPONENT P4 — recipe-attached ("plexiglass_holder_tech_top", modeled in this document).
Construction recipe (the document's own serialized feature program — sketch geometry with constraints, then the solid features built on it; lengths are millimeters unless a unit is written):

FEATURE [PartDesign::CoordinateSystem] Local_CS019
  AttacherType = Attacher::AttachEngine3D
  MapMode = 5
  Support = -> [XY_Plane018]
FEATURE [Sketcher::SketchObject] Sketch121
  FullyConstrained = true
  MapMode = 5
  Support = -> [XY_Plane018]
  sketch-geometry (7):
    g0: ArcOfCircle CenterX=0 CenterY=0 CenterZ=0 NormalX=0 NormalY=0 NormalZ=1 AngleXU=0 Radius=196.875 StartAngle=0.763183 EndAngle=1.5708
    g1: LineSegment StartX=142.27 StartY=136.085 StartZ=0 EndX=150.91 EndY=127.052 EndZ=0
    g2: LineSegment StartX=150.91 StartY=127.052 StartZ=0 EndX=159.551 EndY=118.019 EndZ=0
    g3: LineSegment StartX=159.551 StartY=118.019 StartZ=0 EndX=141.485 EndY=100.739 EndZ=0
    g4: LineSegment StartX=0 StartY=0 StartZ=0 EndX=175.512 EndY=101.332 EndZ=0
    g5: LineSegment StartX=141.485 StartY=100.739 StartZ=0 EndX=124.204 EndY=118.805 EndZ=0
    g6: LineSegment StartX=124.204 StartY=118.805 StartZ=0 EndX=142.27 EndY=136.085 EndZ=0
  constraints (21):
    c: Coincident(g0,g-1)
    c: PointOnObject(g0,g-2)
    c: Coincident(g2,g1)
    c: Parallel(g1,g2)
    c: Equal(g2,g1)
    c: Distance(g2,g0) = 25
    c: Tangent(g1,g0) = 1.5708
    c: DistanceY(g0) = 196.875
    c: Coincident(g3,g2)
    c: Distance(g3) = 25
    c: Coincident(g4,g0)
    c: PointOnObject(g4,g2)
    c: Perpendicular(g2,g3)
    c: Angle(g-1,g4) = 0.523599
    c: Distance(g3,g4) = 16.5
    c: Distance(g2,g4) = 22.4325
    c: Coincident(g5,g3)
    c: Perpendicular(g5,g3)
    c: Coincident(g6,g5)
    c: Coincident(g6,g0)
    c: Perpendicular(g5,g6)
FEATURE [Sketcher::SketchObject] Sketch053
  ExternalGeometry = -> [Sketch121]
  FullyConstrained = true
  MapMode = 5
  Support = -> [XY_Plane018]
  sketch-geometry (7):
    g0: LineSegment StartX=1.11e-14 StartY=181.875 StartZ=0 EndX=1.21e-14 EndY=196.875 EndZ=0
    g1: ArcOfCircle CenterX=0 CenterY=0 CenterZ=0 NormalX=0 NormalY=0 NormalZ=1 AngleXU=0 Radius=181.875 StartAngle=0.768652 EndAngle=1.5708
    g2: ArcOfCircle CenterX=0 CenterY=0 CenterZ=0 NormalX=0 NormalY=0 NormalZ=1 AngleXU=0 Radius=196.875 StartAngle=0.768289 EndAngle=1.5708
    g3: LineSegment StartX=132.151 StartY=126.406 StartZ=0 EndX=141.545 EndY=135.392 EndZ=0
    g4: ArcOfCircle CenterX=140.854 CenterY=136.115 CenterZ=0 NormalX=0 NormalY=0 NormalZ=1 AngleXU=0 Radius=1 StartAngle=5.47557 EndAngle=7.05147
    g5: ArcOfCircle CenterX=131.46 CenterY=127.129 CenterZ=0 NormalX=0 NormalY=0 NormalZ=1 AngleXU=0 Radius=1 StartAngle=3.91024 EndAngle=5.47557
    g6: GeomPoint X=131.43 Y=125.717 Z=0
  constraints (18):
    c: PointOnObject(g0,g-2)
    c: PointOnObject(g0,g-2)
    c: DistanceY(g0) = 196.875
    c: Tangent(g3,g4) = -1.5708
    c: Tangent(g2,g4) = -1.5708
    c: Tangent(g3,g5) = -1.5708
    c: Tangent(g1,g5) = 1.5708
    c: Equal(g5,g4)
    c: Diameter(g5) = 2
    c: Perpendicular(g-3,g3)
    c: PointOnObject(g-3,g3)
    c: Coincident(g2,g0)
    c: Coincident(g1,g0)
    c: PointOnObject(g6,g3)
    c: PointOnObject(g6,g1)
    c: Coincident(g1,g2)
    c: DistanceY(g0,g0) = 15
    c: Coincident(g1,g-1)
FEATURE [PartDesign::Pad] Pad015
  Direction = (0,0,1)
  Length = 3
  Length2 = 10
  Profile = -> Sketch053
  ReferenceAxis = -> Sketch053 [N_Axis]
  Type = 0
FEATURE [PartDesign::Mirrored] Mirrored020
  BaseFeature = -> Pad015
  MirrorPlane = -> Sketch053 [V_Axis]
  Originals = -> [Pad015]
  Refine = true
FEATURE [Sketcher::SketchObject] Sketch054
  ExternalGeometry = -> [Sketch053]
  FullyConstrained = true
  MapMode = 5
  Support = -> [XY_Plane018]
  sketch-geometry (6):
    g0: ArcOfCircle CenterX=0 CenterY=0 CenterZ=0 NormalX=0 NormalY=0 NormalZ=1 AngleXU=0 Radius=189.373 StartAngle=0.763183 EndAngle=1.5708
    g1: Circle CenterX=129.748 CenterY=137.941 CenterZ=0 NormalX=0 NormalY=0 NormalZ=1 AngleXU=0 Radius=1.7
    g2: Circle CenterX=1.16e-14 CenterY=189.373 CenterZ=0 NormalX=0 NormalY=0 NormalZ=1 AngleXU=0 Radius=1.7
    g3: Circle CenterX=-129.748 CenterY=137.941 CenterZ=0 NormalX=0 NormalY=0 NormalZ=1 AngleXU=0 Radius=1.7
    g4: LineSegment StartX=132.151 StartY=126.406 StartZ=0 EndX=136.848 EndY=130.899 EndZ=0
    g5: LineSegment StartX=136.848 StartY=130.899 StartZ=0 EndX=141.545 EndY=135.392 EndZ=0
  constraints (15):
    c: PointOnObject(g1,g0)
    c: Diameter(g1) = 3.4
    c: Coincident(g2,g0)
    c: Equal(g2,g1)
    c: Equal(g3,g1)
    c: Symmetric(g1,g3,g-2)
    c: Coincident(g5,g4)
    c: Equal(g4,g5)
    c: Parallel(g4,g5)
    c: Coincident(g0,g4)
    c: Coincident(g0,g-1)
    c: Distance(g1,g0) = 10
    c: PointOnObject(g2,g-2)
    c: Coincident(g4,g-3)
    c: Coincident(g5,g-3)
FEATURE [PartDesign::Pocket] Pocket018
  BaseFeature = -> Mirrored020
  Direction = (0,0,-1)
  Length = 5
  Length2 = 5
  Midplane = true
  Profile = -> Sketch054
  ReferenceAxis = -> Sketch054 [N_Axis]
  Type = 1
FEATURE [PartDesign::Body] Body001003005003004  label="plexiglass_holder_tech_top"
  Group = -> [Sketch053,Pad015,Mirrored020,Pocket018,Local_CS019,Sketch054,Sketch121]
  Origin = -> Origin017
  Placement = pos=(0,0,0) rot=(0,0,1;1.0472rad)
  Tip = -> Pocket018
COMPONENT P5 — recipe-attached ("basement2", modeled in this document).
Construction recipe (the document's own serialized feature program — sketch geometry with constraints, then the solid features built on it; lengths are millimeters unless a unit is written):

FEATURE [Sketcher::SketchObject] Sketch076
  FullyConstrained = true
  MapMode = 5
  Support = -> [XY_Plane025]
  sketch-geometry (1):
    g0: Circle CenterX=0 CenterY=0 CenterZ=0 NormalX=0 NormalY=0 NormalZ=1 AngleXU=0 Radius=168.5
  constraints (2):
    c: Coincident(g0,g-1)
    c: Diameter(g0) = 337
FEATURE [PartDesign::Pad] Pad020
  Direction = (0,0,1)
  Length = 3
  Length2 = 10
  Profile = -> Sketch076
  ReferenceAxis = -> Sketch076 [N_Axis]
  Type = 0
FEATURE [PartDesign::SubShapeBinder] Binder044
  BindCopyOnChange = 0
  BindMode = 0
  ClaimChildren = false
  Context = -> Body001003005003011 [Binder044.]
  Fuse = false
  MakeFace = true
  OffsetFill = false
  OffsetIntersection = false
  OffsetJoinType = 0
  OffsetOpenResult = false
  PartialLoad = false
  Relative = true
  Support = -> [Body001003005003[Pocket036.Sketch075.]]
  _Version = 2
FEATURE [PartDesign::SubShapeBinder] Binder045
  BindCopyOnChange = 0
  BindMode = 0
  ClaimChildren = false
  Context = -> Body001003005003011 [Binder045.]
  Fuse = false
  MakeFace = true
  OffsetFill = false
  OffsetIntersection = false
  OffsetJoinType = 0
  OffsetOpenResult = false
  PartialLoad = false
  Placement = pos=(0,0,0) rot=(0,0,1;0.785398rad)
  Relative = true
  Support = -> [Body001003005003[Pocket036.Sketch075.]]
  _Version = 2
FEATURE [PartDesign::Pocket] Pocket088
  BaseFeature = -> Pad020
  Direction = (0,0,-1)
  Length = 5
  Length2 = 5
  Midplane = true
  Profile = -> Binder044
  Type = 1
FEATURE [PartDesign::Hole] Hole
  BaseFeature = -> Pocket088
  CustomThreadClearance = 0
  Depth = 25
  DepthType = 0
  Diameter = 15.5
  DrillForDepth = false
  DrillPoint = 1
  DrillPointAngle = 118
  HoleCutCountersinkAngle = 90
  HoleCutCustomValues = false
  HoleCutDepth = 0
  HoleCutDiameter = 6.1
  HoleCutType = 0
  ModelThread = false
  Profile = -> Binder045
  Reversed = true
  Tapered = false
  TaperedAngle = 90
  ThreadClass = 0
  ThreadDepth = 25
  ThreadDepthType = 0
  ThreadDirection = 0
  ThreadFit = 0
  ThreadSize = 0
  ThreadType = 0
  Threaded = false
  UseCustomThreadClearance = false
FEATURE [PartDesign::Body] Body001003005003011  label="basement2"
  Group = -> [Sketch076,Pad020,Binder044,Binder045,Pocket088,Hole]
  Origin = -> Origin024
  Tip = -> Hole
COMPONENT P6 — recipe-attached ("Body001003005003012", modeled in this document).
Construction recipe (the document's own serialized feature program — sketch geometry with constraints, then the solid features built on it; lengths are millimeters unless a unit is written):

FEATURE [Sketcher::SketchObject] Sketch078
  FullyConstrained = true
  MapMode = 5
  Placement = pos=(0,0,0) rot=(1,0,0;1.5708rad)
  Support = -> [XZ_Plane025]
FEATURE [Sketcher::SketchObject] Sketch079
  FullyConstrained = true
  MapMode = 5
  Placement = pos=(0,0,0) rot=(0.57735,0.57735,0.57735;2.0944rad)
  Support = -> [YZ_Plane025]
  sketch-geometry (3):
    g0: LineSegment StartX=15 StartY=0 StartZ=0 EndX=0 EndY=0 EndZ=0
    g1: LineSegment StartX=0 StartY=0 StartZ=0 EndX=0 EndY=157 EndZ=0
    g2: LineSegment StartX=0 StartY=157 StartZ=0 EndX=15 EndY=157 EndZ=0
  constraints (9):
    c: PointOnObject(g0,g-1)
    c: Coincident(g0,g-1)
    c: Coincident(g1,g0)
    c: PointOnObject(g1,g-2)
    c: Coincident(g2,g1)
    c: Horizontal(g2)
    c: DistanceX(g0,g0) = 15
    c: Vertical(g0,g2)
    c: DistanceY(g1) = 157
FEATURE [PartDesign::FeaturePython] BaseBend  # WARN: FeaturePython — macro-defined, semantics opaque (R4)
  BendSide = 0
  BendSketch = -> Sketch079
  MidPlane = true
  Reverse = false
  length = 15
  radius = 2
  thickness = 1
FEATURE [Sketcher::SketchObject] Sketch080
  AttachmentOffset = pos=(0,7.5,0) rot=(0,0,1;0rad)
  FullyConstrained = true
  MapMode = 5
  Placement = pos=(0,7.5,0) rot=(0,0,1;0rad)
  Support = -> [XY_Plane026]
  sketch-geometry (1):
    g0: Circle CenterX=0 CenterY=0 CenterZ=0 NormalX=0 NormalY=0 NormalZ=1 AngleXU=0 Radius=1.65
  constraints (3):
    c: PointOnObject(g0,g-2)
    c: Diameter(g0) = 3.3
    c: DistanceY(g0) = 0
FEATURE [PartDesign::Pocket] Pocket039
  BaseFeature = -> BaseBend
  Direction = (0,0,-1)
  Length = 5
  Length2 = 5
  Profile = -> Sketch080
  ReferenceAxis = -> Sketch080 [N_Axis]
  Reversed = true
  Type = 1
FEATURE [Sketcher::SketchObject] Sketch081
  FullyConstrained = true
  MapMode = 5
  Support = -> [XY_Plane026]
  sketch-geometry (3):
    g0: ArcOfCircle CenterX=4.5 CenterY=12 CenterZ=0 NormalX=0 NormalY=0 NormalZ=1 AngleXU=0 Radius=3 StartAngle=1e-16 EndAngle=1.57079
    g1: LineSegment StartX=4.50001 StartY=15 StartZ=0 EndX=7.5 EndY=15 EndZ=0
    g2: LineSegment StartX=7.5 StartY=12 StartZ=0 EndX=7.5 EndY=15 EndZ=0
  constraints (9):
    c: Diameter(g0) = 6
    c: Coincident(g1,g0)
    c: Tangent(g1,g0)
    c: Coincident(g2,g1)
    c: Vertical(g2)
    c: Horizontal(g1)
    c: DistanceX(g1) = 7.5
    c: DistanceY(g1) = 15
    c: Tangent(g2,g0) = -1.5708
FEATURE [PartDesign::Pocket] Pocket040
  BaseFeature = -> Pocket039
  Direction = (0,0,-1)
  Length = 5
  Length2 = 5
  Midplane = true
  Profile = -> Sketch081
  ReferenceAxis = -> Sketch081 [N_Axis]
  Type = 1
FEATURE [PartDesign::Mirrored] Mirrored028
  BaseFeature = -> Pocket040
  MirrorPlane = -> Sketch081 [V_Axis]
  Originals = -> [Pocket040]
FEATURE [PartDesign::Body] Body001003005003012
  Group = -> [Sketch078,Sketch079,BaseBend,Sketch080,Pocket039,Sketch081,Pocket040,Mirrored028]
  Origin = -> Origin025
  Tip = -> Mirrored028
COMPONENT P7 — recipe-attached ("plexiglass_holder_top", modeled in this document).
Construction recipe (the document's own serialized feature program — sketch geometry with constraints, then the solid features built on it; lengths are millimeters unless a unit is written):

FEATURE [Sketcher::SketchObject] Sketch082
  FullyConstrained = false
  MapMode = 5
  Support = -> [XY_Plane027]
  sketch-geometry (19):
    g0: ArcOfCircle CenterX=0 CenterY=0 CenterZ=0 NormalX=0 NormalY=0 NormalZ=1 AngleXU=0 Radius=196.875 StartAngle=0.650114 EndAngle=1.5708
    g1: LineSegment StartX=1.21e-14 StartY=196.875 StartZ=0 EndX=1.11e-14 EndY=181.875 EndZ=0
    g2: ArcOfCircle CenterX=0 CenterY=0 CenterZ=0 NormalX=0 NormalY=0 NormalZ=1 AngleXU=0 Radius=181.875 StartAngle=0.650114 EndAngle=1.5708
    g3: ArcOfCircle CenterX=150.746 CenterY=114.625 CenterZ=0 NormalX=0 NormalY=0 NormalZ=1 AngleXU=0 Radius=7.5 StartAngle=3.79171 EndAngle=6.9333
    g4: LineSegment StartX=0 StartY=0 StartZ=0 EndX=164.625 EndY=95.0465 EndZ=0
    g5: GeomPoint X=155.166 Y=108.566 Z=0
    g6: LineSegment StartX=164.625 StartY=95.0465 StartZ=0 EndX=155.166 EndY=108.566 EndZ=0
    g7: ArcOfCircle CenterX=0 CenterY=0 CenterZ=0 NormalX=0 NormalY=0 NormalZ=1 AngleXU=0 Radius=189.375 StartAngle=0.610508 EndAngle=1.5708
    g8: ArcOfCircle CenterX=0 CenterY=0 CenterZ=0 NormalX=0 NormalY=0 NormalZ=1 AngleXU=0 Radius=189.375 StartAngle=0.645052 EndAngle=1.5708
    g9: ArcOfCircle CenterX=0 CenterY=0 CenterZ=0 NormalX=0 NormalY=0 NormalZ=1 AngleXU=0 Radius=196.875 StartAngle=0.612741 EndAngle=0.650114
    g10: LineSegment StartX=155.166 StartY=108.566 StartZ=0 EndX=160.741 EndY=111.784 EndZ=0
    g11: ArcOfCircle CenterX=160.241 CenterY=112.65 CenterZ=0 NormalX=0 NormalY=0 NormalZ=1 AngleXU=0 Radius=1 StartAngle=5.23599 EndAngle=6.89593
    g12: ArcOfCircle CenterX=0 CenterY=0 CenterZ=0 NormalX=0 NormalY=0 NormalZ=1 AngleXU=0 Radius=181.875 StartAngle=0.619097 EndAngle=0.650114
    g13: LineSegment StartX=155.166 StartY=108.566 StartZ=0 EndX=149.434 EndY=105.257 EndZ=0
    g14: ArcOfCircle CenterX=148.934 CenterY=106.123 CenterZ=0 NormalX=0 NormalY=0 NormalZ=1 AngleXU=0 Radius=1 StartAngle=3.76069 EndAngle=5.23599
    g15: ArcOfCircle CenterX=0 CenterY=0 CenterZ=0 NormalX=0 NormalY=0 NormalZ=1 AngleXU=0 Radius=196.875 StartAngle=0.597316 EndAngle=1.5708
    g16: LineSegment StartX=162.786 StartY=110.728 StartZ=0 EndX=0 EndY=0 EndZ=0
    g17: LineSegment StartX=162.786 StartY=110.728 StartZ=0 EndX=0 EndY=110.728 EndZ=0
    g18: LineSegment StartX=0 StartY=0 StartZ=0 EndX=162.786 EndY=110.728 EndZ=0
  constraints (52):
    c: Coincident(g0,g-1)
    c: PointOnObject(g0,g-2)
    c: DistanceY(g0) = 196.875
    c: Coincident(g1,g0)
    c: PointOnObject(g1,g-2)
    c: Coincident(g2,g0)
    c: Coincident(g2,g1)
    c: Tangent(g3,g0) = -1.5708
    c: Tangent(g3,g2) = 1.5708
    c: DistanceY(g1,g1) = 15
    c: Coincident(g4,g0)
    c: Angle(g-1,g4) = 0.523599
    c: PointOnObject(g5,g3)
    c: Coincident(g6,g4)
    c: Coincident(g6,g5)
    c: Coincident(g7,g0)
    c: Coincident(g7,g5)
    c: PointOnObject(g7,g1)
    c: PointOnObject(g3,g7)
    c: Tangent(g6,g7)
    c: Distance(g6) = 16.5
    c: Coincident(g8,g0)
    c: PointOnObject(g8,g-2)
    c: DistanceY(g8,g0) = 7.5
    c: Coincident(g9,g0)
    c: Coincident(g9,g0)
    c: Coincident(g10,g5)
    c: Parallel(g10,g4)
    c: Tangent(g9,g11) = -1.5708
    c: Tangent(g10,g11) = -1.5708
    c: Diameter(g11) = 2
    c: Coincident(g12,g0)
    c: Coincident(g12,g2)
    c: Coincident(g13,g10)
    c: Parallel(g13,g10)
    c: Tangent(g12,g14) = 1.5708
    c: Tangent(g13,g14) = 1.5708
    c: Equal(g14,g11)
    c: Coincident(g15,g0)
    c: PointOnObject(g15,g-2)
    c: Equal(g15,g9)
    c: Distance(g15,g4) = 14.5
    c: Coincident(g16,g15)
    c: Coincident(g16,g0)
    c: Angle(g16,g-2) = 0.97348
    c: Coincident(g17,g15)
    c: PointOnObject(g17,g-2)
    c: Horizontal(g17)
    c: DistanceX(g17,g17) = 162.786
    c: Coincident(g18,g0)
    c: Coincident(g18,g15)
    c: Angle(g16,g-2) = 0.97348
FEATURE [PartDesign::Pad] Pad021
  Direction = (0,0,1)
  Length = 3
  Length2 = 10
  Profile = -> Sketch082
  ReferenceAxis = -> Sketch082 [N_Axis]
  Type = 0
FEATURE [Sketcher::SketchObject] Sketch083
  FullyConstrained = true
  MapMode = 5
  Support = -> [XY_Plane027]
  sketch-geometry (11):
    g0: ArcOfCircle CenterX=0 CenterY=0 CenterZ=0 NormalX=0 NormalY=0 NormalZ=1 AngleXU=0 Radius=196.875 StartAngle=0.650114 EndAngle=1.5708
    g1: LineSegment StartX=1.21e-14 StartY=196.875 StartZ=0 EndX=1.11e-14 EndY=181.875 EndZ=0
    g2: ArcOfCircle CenterX=0 CenterY=0 CenterZ=0 NormalX=0 NormalY=0 NormalZ=1 AngleXU=0 Radius=181.875 StartAngle=0.650114 EndAngle=1.5708
    g3: ArcOfCircle CenterX=150.746 CenterY=114.625 CenterZ=0 NormalX=0 NormalY=0 NormalZ=1 AngleXU=0 Radius=7.5 StartAngle=3.79171 EndAngle=6.9333
    g4: LineSegment StartX=0 StartY=0 StartZ=0 EndX=164.625 EndY=95.0465 EndZ=0
    g5: GeomPoint X=155.166 Y=108.566 Z=0
    g6: LineSegment StartX=164.625 StartY=95.0465 StartZ=0 EndX=155.166 EndY=108.566 EndZ=0
    g7: ArcOfCircle CenterX=0 CenterY=0 CenterZ=0 NormalX=0 NormalY=0 NormalZ=1 AngleXU=0 Radius=189.375 StartAngle=0.610508 EndAngle=1.5708
    g8: ArcOfCircle CenterX=0 CenterY=0 CenterZ=0 NormalX=0 NormalY=0 NormalZ=1 AngleXU=0 Radius=189.375 StartAngle=0.663319 EndAngle=1.5708
    g9: Circle CenterX=149.219 CenterY=116.605 CenterZ=0 NormalX=0 NormalY=0 NormalZ=1 AngleXU=0 Radius=1.7
    g10: Circle CenterX=-149.219 CenterY=116.605 CenterZ=0 NormalX=0 NormalY=0 NormalZ=1 AngleXU=0 Radius=1.7
  constraints (29):
    c: Coincident(g0,g-1)
    c: PointOnObject(g0,g-2)
    c: DistanceY(g0) = 196.875
    c: Coincident(g1,g0)
    c: PointOnObject(g1,g-2)
    c: Coincident(g2,g0)
    c: Coincident(g2,g1)
    c: Tangent(g3,g0) = -1.5708
    c: Tangent(g3,g2) = 1.5708
    c: DistanceY(g1,g1) = 15
    c: Coincident(g4,g0)
    c: Angle(g-1,g4) = 0.523599
    c: PointOnObject(g5,g3)
    c: Coincident(g6,g4)
    c: Coincident(g6,g5)
    c: Coincident(g7,g0)
    c: Coincident(g7,g5)
    c: PointOnObject(g7,g1)
    c: PointOnObject(g3,g7)
    c: Tangent(g6,g7)
    c: Distance(g6) = 16.5
    c: Coincident(g8,g0)
    c: PointOnObject(g8,g-2)
    c: DistanceY(g8,g0) = 7.5
    c: Coincident(g9,g8)
    c: Diameter(g9) = 3.4
    c: Symmetric(g10,g9,g-2)
    c: Equal(g10,g9)
    c: Distance(g5,g9) = 10
FEATURE [PartDesign::Mirrored] Mirrored029
  BaseFeature = -> Pad021
  MirrorPlane = -> Sketch082 [V_Axis]
  Originals = -> [Pad021]
  Refine = true
FEATURE [PartDesign::Pocket] Pocket041
  BaseFeature = -> Mirrored029
  Direction = (0,0,-1)
  Length = 5
  Length2 = 5
  Midplane = true
  Profile = -> Sketch083
  ReferenceAxis = -> Sketch083 [N_Axis]
  Type = 1
FEATURE [Sketcher::SketchObject] Sketch084
  FullyConstrained = true
  MapMode = 5
  Support = -> [XY_Plane027]
  sketch-geometry (15):
    g0: ArcOfCircle CenterX=0 CenterY=0 CenterZ=0 NormalX=0 NormalY=0 NormalZ=1 AngleXU=0 Radius=196.875 StartAngle=0.650114 EndAngle=1.5708
    g1: LineSegment StartX=1.21e-14 StartY=196.875 StartZ=0 EndX=1.11e-14 EndY=181.875 EndZ=0
    g2: ArcOfCircle CenterX=0 CenterY=0 CenterZ=0 NormalX=0 NormalY=0 NormalZ=1 AngleXU=0 Radius=181.875 StartAngle=0.650114 EndAngle=1.5708
    g3: ArcOfCircle CenterX=150.746 CenterY=114.625 CenterZ=0 NormalX=0 NormalY=0 NormalZ=1 AngleXU=0 Radius=7.5 StartAngle=3.79171 EndAngle=6.9333
    g4: LineSegment StartX=0 StartY=0 StartZ=0 EndX=164.625 EndY=95.0465 EndZ=0
    g5: GeomPoint X=155.166 Y=108.566 Z=0
    g6: LineSegment StartX=164.625 StartY=95.0465 StartZ=0 EndX=155.166 EndY=108.566 EndZ=0
    g7: ArcOfCircle CenterX=0 CenterY=0 CenterZ=0 NormalX=0 NormalY=0 NormalZ=1 AngleXU=0 Radius=189.375 StartAngle=0.610508 EndAngle=1.5708
    g8: ArcOfCircle CenterX=0 CenterY=0 CenterZ=0 NormalX=0 NormalY=0 NormalZ=1 AngleXU=0 Radius=196.875 StartAngle=0.612741 EndAngle=0.650114
    g9: LineSegment StartX=155.166 StartY=108.566 StartZ=0 EndX=160.741 EndY=111.784 EndZ=0
    g10: ArcOfCircle CenterX=160.241 CenterY=112.65 CenterZ=0 NormalX=0 NormalY=0 NormalZ=1 AngleXU=0 Radius=1 StartAngle=5.23599 EndAngle=6.89593
    g11: ArcOfCircle CenterX=0 CenterY=0 CenterZ=0 NormalX=0 NormalY=0 NormalZ=1 AngleXU=0 Radius=181.875 StartAngle=0.619097 EndAngle=0.650114
    g12: LineSegment StartX=155.166 StartY=108.566 StartZ=0 EndX=149.434 EndY=105.257 EndZ=0
    g13: ArcOfCircle CenterX=148.934 CenterY=106.123 CenterZ=0 NormalX=0 NormalY=0 NormalZ=1 AngleXU=0 Radius=1 StartAngle=3.76069 EndAngle=5.23599
    g14: Circle CenterX=1.16e-14 CenterY=189.375 CenterZ=0 NormalX=0 NormalY=0 NormalZ=1 AngleXU=0 Radius=1.7
  constraints (37):
    c: Coincident(g0,g-1)
    c: PointOnObject(g0,g-2)
    c: DistanceY(g0) = 196.875
    c: Coincident(g1,g0)
    c: PointOnObject(g1,g-2)
    c: Coincident(g2,g0)
    c: Coincident(g2,g1)
    c: Tangent(g3,g0) = -1.5708
    c: Tangent(g3,g2) = 1.5708
    c: DistanceY(g1,g1) = 15
    c: Coincident(g4,g0)
    c: Angle(g-1,g4) = 0.523599
    c: PointOnObject(g5,g3)
    c: Coincident(g6,g4)
    c: Coincident(g6,g5)
    c: Coincident(g7,g0)
    c: Coincident(g7,g5)
    c: PointOnObject(g7,g1)
    c: PointOnObject(g3,g7)
    c: Tangent(g6,g7)
    c: Distance(g6) = 16.5
    c: Coincident(g8,g0)
    c: Coincident(g8,g0)
    c: Coincident(g9,g5)
    c: Parallel(g9,g4)
    c: Tangent(g8,g10) = -1.5708
    c: Tangent(g9,g10) = -1.5708
    c: Diameter(g10) = 2
    c: Coincident(g11,g0)
    c: Coincident(g11,g2)
    c: Coincident(g12,g9)
    c: Parallel(g12,g9)
    c: Tangent(g11,g13) = 1.5708
    c: Tangent(g12,g13) = 1.5708
    c: Equal(g13,g10)
    c: Coincident(g14,g7)
    c: Diameter(g14) = 3.4
FEATURE [PartDesign::Pocket] Pocket042
  BaseFeature = -> Pocket041
  Direction = (0,0,-1)
  Length = 5
  Length2 = 5
  Midplane = true
  Profile = -> Sketch084
  ReferenceAxis = -> Sketch084 [N_Axis]
  Type = 1
FEATURE [PartDesign::Body] Body001003005003013  label="plexiglass_holder_top"
  Group = -> [Sketch082,Pad021,Sketch083,Mirrored029,Pocket041,Sketch084,Pocket042]
  Origin = -> Origin026
  Placement = pos=(0,0,0) rot=(0,0,1;1.0472rad)
  Tip = -> Pocket042
COMPONENT P8 — recipe-attached ("basin_cover_back_material_0.30ansi", modeled in this document).
Construction recipe (the document's own serialized feature program — sketch geometry with constraints, then the solid features built on it; lengths are millimeters unless a unit is written):

FEATURE [PartDesign::SubShapeBinder] Binder020
  BindCopyOnChange = 0
  BindMode = 0
  ClaimChildren = false
  Context = -> Body001003005003014 [Binder020.]
  Fuse = false
  MakeFace = true
  OffsetFill = false
  OffsetIntersection = false
  OffsetJoinType = 0
  OffsetOpenResult = false
  PartialLoad = false
  Relative = false
  Support = -> [Body001003005003003[Pocket019.Sketch055.]]
  _Version = 2
FEATURE [PartDesign::SubShapeBinder] Binder021
  BindCopyOnChange = 0
  BindMode = 0
  ClaimChildren = false
  Context = -> Body001003005003014 [Binder021.]
  Fuse = false
  MakeFace = true
  OffsetFill = false
  OffsetIntersection = false
  OffsetJoinType = 0
  OffsetOpenResult = false
  PartialLoad = false
  Relative = false
  Support = -> [Body001003005003004[Pocket018.Sketch054.]]
  _Version = 2
FEATURE [PartDesign::CoordinateSystem] Local_CS027
  AttacherType = Attacher::AttachEngine3D
  MapMode = 5
  Support = -> [XY_Plane028]
FEATURE [PartDesign::CoordinateSystem] Local_CS028
  AttacherType = Attacher::AttachEngine3D
  AttachmentOffset = pos=(0,0,0) rot=(0,0,1;0.523599rad)
  MapMode = 5
  Placement = pos=(0,0,0) rot=(0,0,1;0.523599rad)
  Support = -> [XY_Plane028]
FEATURE [PartDesign::Plane] DatumPlane023
  Length = 81.9615
  MapMode = 5
  Placement = pos=(0,0,0) rot=(0,0,1;0.523599rad)
  ResizeMode = 0
  Support = -> [Local_CS028]
  Width = 81.9615
FEATURE [PartDesign::CoordinateSystem] Local_CS029
  AttacherType = Attacher::AttachEngine3D
  AttachmentOffset = pos=(0,16.7432,0) rot=(0,0,1;0.523599rad)
  MapMode = 5
  Placement = pos=(0,16.7432,0) rot=(0,0,1;0.523599rad)
  Support = -> [XY_Plane028]
FEATURE [PartDesign::Pad] Pad022
  Direction = (0,0,1)
  Length = 3
  Length2 = 10
  Profile = -> Sketch047
  ReferenceAxis = -> Sketch047 [N_Axis]
  Type = 0
FEATURE [PartDesign::Pocket] Pocket045
  BaseFeature = -> Pad022
  Direction = (0,0,-1)
  Length = 5
  Length2 = 5
  Midplane = true
  Profile = -> Binder021
  Type = 1
FEATURE [PartDesign::SubShapeBinder] Binder037
  BindCopyOnChange = 0
  BindMode = 0
  ClaimChildren = false
  Context = -> Body001003005003014 [Binder037.]
  Fuse = false
  MakeFace = true
  OffsetFill = false
  OffsetIntersection = false
  OffsetJoinType = 0
  OffsetOpenResult = false
  PartialLoad = false
  Relative = false
  Support = -> [Body001003005003004[Sketch121.Edge2]]
  _Version = 2
FEATURE [PartDesign::CoordinateSystem] Local_CS040
  AttacherType = Attacher::AttachEngine3D
  AttachmentOffset = pos=(0,0,0) rot=(-0.57735,-0.57735,-0.57735;2.0944rad)
  MapMode = 7
  Placement = pos=(150.91,127.052,0) rot=(0,0,1;2.33398rad)
  Support = -> [Binder037]
FEATURE [PartDesign::SubShapeBinder] Binder038
  BindCopyOnChange = 0
  BindMode = 0
  ClaimChildren = false
  Context = -> Body001003005003014 [Binder038.]
  Fuse = false
  MakeFace = true
  OffsetFill = false
  OffsetIntersection = false
  OffsetJoinType = 0
  OffsetOpenResult = false
  PartialLoad = false
  Placement = pos=(150.91,127.052,0) rot=(0,0,1;2.33398rad)
  Relative = true
  Support = -> [tech_pillar[Pocket071.Sketch117.]]
  _Version = 2
FEATURE [PartDesign::Pocket] Pocket059
  BaseFeature = -> Pocket045
  Direction = (0,0,-1)
  Length = 5
  Length2 = 5
  Midplane = true
  Profile = -> Binder038
  Type = 1
FEATURE [PartDesign::SubShapeBinder] Binder047
  BindCopyOnChange = 0
  BindMode = 0
  ClaimChildren = false
  Context = -> Body001003005003014 [Binder047.]
  Fuse = false
  MakeFace = true
  OffsetFill = false
  OffsetIntersection = false
  OffsetJoinType = 0
  OffsetOpenResult = false
  PartialLoad = false
  Placement = pos=(104.99,73.8951,1.5) rot=(0,0,1;0.523599rad)
  Relative = false
  Support = -> [Body001[Sketch073.]]
  _Version = 2
FEATURE [PartDesign::CoordinateSystem] Local_CS045
  AttacherType = Attacher::AttachEngine3D
  AttachmentOffset = pos=(119.5,-3,1.5) rot=(0,0,1;0rad)
  MapMode = 5
  Placement = pos=(104.99,73.8951,1.5) rot=(0,0,1;0.523599rad)
  Support = -> [Local_CS029]
FEATURE [PartDesign::Hole] Hole001
  BaseFeature = -> Pocket059
  CustomThreadClearance = 0
  Depth = 25
  DepthType = 0
  Diameter = 6.5
  DrillForDepth = false
  DrillPoint = 1
  DrillPointAngle = 118
  HoleCutCountersinkAngle = 90
  HoleCutCustomValues = false
  HoleCutDepth = 0
  HoleCutDiameter = 6.1
  HoleCutType = 0
  ModelThread = false
  Profile = -> Binder047
  Reversed = true
  Tapered = false
  TaperedAngle = 90
  ThreadClass = 0
  ThreadDepth = 25
  ThreadDepthType = 0
  ThreadDirection = 0
  ThreadFit = 0
  ThreadSize = 0
  ThreadType = 0
  Threaded = false
  UseCustomThreadClearance = false
FEATURE [PartDesign::Mirrored] Mirrored031
  BaseFeature = -> Hole001
  MirrorPlane = -> Sketch047 [V_Axis]
  Originals = -> [Pad022,Pocket045,Pocket059,Hole001]
  Refine = true
FEATURE [PartDesign::Body] Body001003005003014  label="basin_cover_back_material_0.30ansi"
  Group = -> [Pad022,Binder021,Binder020,Pocket045,Pocket059,Hole001,Mirrored031,Local_CS027,Local_CS028,DatumPlane023,Local_CS029,Binder037,Local_CS040,Binder038,Binder047,Local_CS045]
  Origin = -> Origin027
  Tip = -> Mirrored031
COMPONENT P9 — recipe-attached ("corner_72x15_material_0.30ansi", modeled in this document).
Construction recipe (the document's own serialized feature program — sketch geometry with constraints, then the solid features built on it; lengths are millimeters unless a unit is written):

FEATURE [Sketcher::SketchObject] Sketch085
  FullyConstrained = true
  MapMode = 5
  Placement = pos=(0,0,0) rot=(0.57735,0.57735,0.57735;2.0944rad)
  Support = -> [YZ_Plane028]
  sketch-geometry (2):
    g0: LineSegment StartX=0 StartY=23 StartZ=0 EndX=0 EndY=0 EndZ=0
    g1: LineSegment StartX=0 StartY=0 StartZ=0 EndX=23 EndY=0 EndZ=0
  constraints (6):
    c: PointOnObject(g0,g-2)
    c: Coincident(g0,g-1)
    c: Coincident(g1,g0)
    c: PointOnObject(g1,g-1)
    c: Equal(g1,g0)
    c: DistanceX(g1,g1) = 23  'length'
FEATURE [PartDesign::FeaturePython] BaseBend002  # WARN: FeaturePython — macro-defined, semantics opaque (R4)
  BendSide = 0
  BendSketch = -> Sketch085
  MidPlane = true
  Reverse = false
  length = 86
  radius = 2
  thickness = 0.5
FEATURE [Sketcher::SketchObject] Sketch086
  AttachmentOffset = pos=(43,23,0) rot=(0,0,1;0rad)
  FullyConstrained = true
  MapMode = 5
  Placement = pos=(43,23,0) rot=(0,0,1;0rad)
  Support = -> [XY_Plane029]
  sketch-geometry (3):
    g0: ArcOfCircle CenterX=-7.5 CenterY=-7.5 CenterZ=0 NormalX=0 NormalY=0 NormalZ=1 AngleXU=0 Radius=7.5 StartAngle=0 EndAngle=1.5708
    g1: LineSegment StartX=0 StartY=-7.5 StartZ=0 EndX=0 EndY=0 EndZ=0
    g2: LineSegment StartX=0 StartY=0 StartZ=0 EndX=-7.50003 EndY=-6.21876e-11 EndZ=0
  constraints (8):
    c: PointOnObject(g0,g-2)
    c: PointOnObject(g0,g-1)
    c: Coincident(g1,g-1)
    c: Coincident(g2,g1)
    c: Coincident(g2,g0)
    c: Tangent(g2,g0)
    c: Tangent(g1,g0) = -1.5708
    c: Diameter(g0) = 15
FEATURE [PartDesign::Pocket] Pocket047
  BaseFeature = -> BaseBend002
  Direction = (0,0,-1)
  Length = 5
  Length2 = 5
  Midplane = true
  Profile = -> Sketch086
  ReferenceAxis = -> Sketch086 [N_Axis]
  Type = 1
FEATURE [PartDesign::Mirrored] Mirrored032
  MirrorPlane = -> YZ_Plane028
FEATURE [PartDesign::PolarPattern] PolarPattern010
  Angle = 90
  Axis = -> X_Axis028
  Occurrences = 2
FEATURE [PartDesign::MultiTransform] MultiTransform011
  BaseFeature = -> Pocket047
  Originals = -> [Pocket047]
  Transformations = -> [Mirrored032,PolarPattern010]
FEATURE [Sketcher::SketchObject] Sketch087
  AttachmentOffset = pos=(0,14.5,0) rot=(0,0,1;0rad)
  FullyConstrained = true
  MapMode = 5
  Placement = pos=(0,14.5,0) rot=(0,0,1;0rad)
  Support = -> [XY_Plane029]
  sketch-geometry (2):
    g0: Circle CenterX=36 CenterY=0 CenterZ=0 NormalX=0 NormalY=0 NormalZ=1 AngleXU=0 Radius=1.7
    g1: Circle CenterX=-36 CenterY=0 CenterZ=0 NormalX=0 NormalY=0 NormalZ=1 AngleXU=0 Radius=1.7
  constraints (5):
    c: PointOnObject(g0,g-1)
    c: Symmetric(g1,g0,g-1)
    c: Equal(g0,g1)
    c: Diameter(g0) = 3.4
    c: DistanceX(g1,g0) = 72
FEATURE [PartDesign::Pocket] Pocket048
  BaseFeature = -> MultiTransform011
  Direction = (0,0,-1)
  Length = 5
  Length2 = 5
  Midplane = true
  Profile = -> Sketch087
  ReferenceAxis = -> Sketch087 [N_Axis]
  Type = 1
FEATURE [PartDesign::PolarPattern] PolarPattern011
  Angle = 90
  Axis = -> X_Axis028
  BaseFeature = -> Pocket048
  Occurrences = 2
  Originals = -> [Pocket048]
FEATURE [PartDesign::CoordinateSystem] Local_CS031
  AttacherType = Attacher::AttachEngine3D
  MapMode = 2
  Placement = pos=(0,14.5,0) rot=(0,0,1;0rad)
  Support = -> [Sketch087]
FEATURE [PartDesign::Body] Body001003005003015  label="corner_72x15_material_0.30ansi"
  Group = -> [Sketch085,BaseBend002,Sketch086,Pocket047,MultiTransform011,Mirrored032,PolarPattern010,Sketch087,Pocket048,PolarPattern011,Local_CS031]
  Origin = -> Origin028
  Tip = -> PolarPattern011
COMPONENT P10 — recipe-attached ("corner_5.5_material_0.30ansi", modeled in this document).
Construction recipe (the document's own serialized feature program — sketch geometry with constraints, then the solid features built on it; lengths are millimeters unless a unit is written):

FEATURE [PartDesign::Mirrored] Mirrored039
  MirrorPlane = -> YZ_Plane036
FEATURE [PartDesign::PolarPattern] PolarPattern014
  Angle = 90
  Axis = -> X_Axis036
  Occurrences = 2
FEATURE [Sketcher::SketchObject] Sketch108
  FullyConstrained = true
  MapMode = 5
  Placement = pos=(0,0,0) rot=(0.57735,0.57735,0.57735;2.0944rad)
  Support = -> [YZ_Plane036]
  sketch-geometry (2):
    g0: LineSegment StartX=0 StartY=23 StartZ=0 EndX=0 EndY=0 EndZ=0
    g1: LineSegment StartX=0 StartY=0 StartZ=0 EndX=23 EndY=0 EndZ=0
  constraints (6):
    c: PointOnObject(g0,g-2)
    c: Coincident(g0,g-1)
    c: Coincident(g1,g0)
    c: PointOnObject(g1,g-1)
    c: Equal(g1,g0)
    c: DistanceX(g1,g1) = 23  'length'
FEATURE [PartDesign::FeaturePython] BaseBend007  # WARN: FeaturePython — macro-defined, semantics opaque (R4)
  BendSide = 0
  BendSketch = -> Sketch108
  MidPlane = true
  Reverse = false
  length = 86
  radius = 2
  thickness = 0.5
FEATURE [Sketcher::SketchObject] Sketch109
  AttachmentOffset = pos=(43,23,0) rot=(0,0,1;0rad)
  FullyConstrained = true
  MapMode = 5
  Placement = pos=(43,23,0) rot=(0,0,1;0rad)
  Support = -> [XY_Plane037]
  sketch-geometry (3):
    g0: ArcOfCircle CenterX=-7.5 CenterY=-7.5 CenterZ=0 NormalX=0 NormalY=0 NormalZ=1 AngleXU=0 Radius=7.5 StartAngle=0 EndAngle=1.5708
    g1: LineSegment StartX=0 StartY=-7.5 StartZ=0 EndX=0 EndY=0 EndZ=0
    g2: LineSegment StartX=0 StartY=0 StartZ=0 EndX=-7.50003 EndY=-6.21876e-11 EndZ=0
  constraints (8):
    c: PointOnObject(g0,g-2)
    c: PointOnObject(g0,g-1)
    c: Coincident(g1,g-1)
    c: Coincident(g2,g1)
    c: Coincident(g2,g0)
    c: Tangent(g2,g0)
    c: Tangent(g1,g0) = -1.5708
    c: Diameter(g0) = 15
FEATURE [PartDesign::Pocket] Pocket063
  BaseFeature = -> BaseBend007
  Direction = (0,0,-1)
  Length = 5
  Length2 = 5
  Midplane = true
  Profile = -> Sketch109
  ReferenceAxis = -> Sketch109 [N_Axis]
  Type = 1
FEATURE [PartDesign::MultiTransform] MultiTransform013
  BaseFeature = -> Pocket063
  Originals = -> [Pocket063]
  Transformations = -> [Mirrored039,PolarPattern014]
FEATURE [Sketcher::SketchObject] Sketch110
  AttachmentOffset = pos=(0,14.5,0) rot=(0,0,1;0rad)
  FullyConstrained = true
  MapMode = 5
  Placement = pos=(0,-3.2e-15,14.5) rot=(1,0,0;1.5708rad)
  Support = -> [XZ_Plane036]
  sketch-geometry (2):
    g0: Circle CenterX=36 CenterY=0 CenterZ=0 NormalX=0 NormalY=0 NormalZ=1 AngleXU=0 Radius=1.7
    g1: Circle CenterX=-36 CenterY=0 CenterZ=0 NormalX=0 NormalY=0 NormalZ=1 AngleXU=0 Radius=1.7
  constraints (5):
    c: PointOnObject(g0,g-1)
    c: Symmetric(g1,g0,g-1)
    c: Equal(g0,g1)
    c: Diameter(g0) = 3.4
    c: DistanceX(g1,g0) = 72
FEATURE [PartDesign::CoordinateSystem] Local_CS034
  AttacherType = Attacher::AttachEngine3D
  MapMode = 2
  Placement = pos=(0,-3.2e-15,14.5) rot=(1,0,0;1.5708rad)
  Support = -> [Sketch110]
FEATURE [PartDesign::Pocket] Pocket064
  BaseFeature = -> MultiTransform013
  Direction = (0,1,2e-16)
  Length = 5
  Length2 = 5
  Midplane = true
  Profile = -> Sketch110
  ReferenceAxis = -> Sketch110 [N_Axis]
  Type = 1
FEATURE [Sketcher::SketchObject] Sketch111
  AttachmentOffset = pos=(0,14.5,0) rot=(0,0,1;0rad)
  FullyConstrained = true
  MapMode = 5
  Placement = pos=(0,14.5,0) rot=(0,0,1;0rad)
  Support = -> [XY_Plane037]
  sketch-geometry (2):
    g0: Circle CenterX=36 CenterY=0 CenterZ=0 NormalX=0 NormalY=0 NormalZ=1 AngleXU=0 Radius=2.75
    g1: Circle CenterX=-36 CenterY=0 CenterZ=0 NormalX=0 NormalY=0 NormalZ=1 AngleXU=0 Radius=2.75
  constraints (5):
    c: PointOnObject(g0,g-1)
    c: Symmetric(g1,g0,g-1)
    c: Equal(g0,g1)
    c: Diameter(g0) = 5.5
    c: DistanceX(g1,g0) = 72
FEATURE [PartDesign::Pocket] Pocket065
  BaseFeature = -> Pocket064
  Direction = (0,0,-1)
  Length = 5
  Length2 = 5
  Midplane = true
  Profile = -> Sketch111
  ReferenceAxis = -> Sketch111 [N_Axis]
  Type = 1
FEATURE [PartDesign::Body] Body001003005003015002  label="corner_5.5_material_0.30ansi"
  Group = -> [Sketch108,BaseBend007,Sketch109,Pocket063,MultiTransform013,Mirrored039,PolarPattern014,Sketch110,Pocket064,Local_CS034,Sketch111,Pocket065]
  Origin = -> Origin036
  Tip = -> Pocket065
COMPONENT P11 — recipe-attached ("Body001003005003015006", modeled in this document).
Construction recipe (the document's own serialized feature program — sketch geometry with constraints, then the solid features built on it; lengths are millimeters unless a unit is written):

FEATURE [PartDesign::CoordinateSystem] Local_CS046
  AttacherType = Attacher::AttachEngine3D
  AttachmentOffset = pos=(0,0,0) rot=(0,0,1;0.523599rad)
  MapMode = 5
  Placement = pos=(0,0,0) rot=(0,0,1;0.523599rad)
  Support = -> [XY_Plane046]
FEATURE [Part::Part2DObjectPython] Line  # Draft 2D object (typed FeaturePython)
  AnglePlaneMid = 5.71059
  AnglePlaneSide = 2.86241
  Area = 0
  AttachmentOffset = pos=(200,0,10) rot=(0,0,1;0rad)
  ChamferSize = 0
  Closed = true
  End = (0,0,0)
  FilletRadius = 0
  Length = 200.25
  MakeFace = true
  MapMode = 2
  Placement = pos=(173.205,100,10) rot=(0,0,1;0.523599rad)
  Points = (2) [(0,0,0),(-200,0,-10)]
  Start = (173.205,100,10)
  Subdivisions = 0
  Support = -> [Local_CS046]
  expr: .AttachmentOffset.Base.x = <<main>>.work_plane_width
  expr: AnglePlaneMid = atan2(.Start.z; .Start.y)
  expr: AnglePlaneSide = atan2(.Start.z; hypot(.Start.x; .Start.y))
  expr: End = Local_CS046.Placement.Base
  expr: Support = Local_CS046._self
FEATURE [Sketcher::SketchObject] Sketch142
  FullyConstrained = true
  MapMode = 5
  Support = -> [XY_Plane046]
FEATURE [Sketcher::SketchObject] Sketch143
  AttachmentOffset = pos=(0,0,0) rot=(0,1,0;0.523599rad)
  ExternalGeometry = -> [Line]
  FullyConstrained = true
  MapMode = 5
  Placement = pos=(0,0,0) rot=(0.935113,0.250563,0.250563;1.63783rad)
  Support = -> [XZ_Plane045]
  constraints (1):
    c: Angle(g-1,g-3) = 0.0499584
FEATURE [PartDesign::Line] DatumLine
  AttacherType = Attacher::AttachEngineLine
  Length = 20
  MapMode = 24
  Placement = pos=(173.205,100,10) rot=(0.57735,-0.57735,-0.57735;2.0944rad)
  ResizeMode = 0
  Support = -> [Line,X_Axis045]
FEATURE [PartDesign::CoordinateSystem] Local_CS047
  AttacherType = Attacher::AttachEngine3D
  AttachmentOffset = pos=(0,0,0) rot=(0,1,0;-0.049958rad)
  MapMode = 5
  Placement = pos=(0,0,0) rot=(-0.024869,0.092812,-0.995373;5.75726rad)
  Support = -> [Local_CS046]
  expr: .AttachmentOffset.Rotation.Angle = -Line.AnglePlaneSide
FEATURE [Sketcher::SketchObject] Sketch144
  AttachmentOffset = pos=(0,0,0) rot=(0.57735,0.57735,0.57735;2.0944rad)
  ExternalGeometry = -> [DatumLine]
  FullyConstrained = true
  MapMode = 5
  Placement = pos=(0,0,0) rot=(0.369727,0.640387,0.673206;2.40018rad)
  Support = -> [Local_CS047]
  expr: Support = Local_CS047._self
  sketch-geometry (3):
    g0: LineSegment StartX=0 StartY=0 StartZ=0 EndX=20 EndY=1.72989 EndZ=0
    g1: LineSegment StartX=20 StartY=1.72989 StartZ=0 EndX=20 EndY=0 EndZ=0
    g2: LineSegment StartX=20 StartY=0 StartZ=0 EndX=0 EndY=0 EndZ=0
  constraints (9):
    c: Coincident(g0,g-1)
    c: PointOnObject(g0,g-3)
    c: Coincident(g1,g0)
    c: PointOnObject(g1,g-1)
    c: Vertical(g1)
    c: Coincident(g2,g1)
    c: Coincident(g2,g0)
    c: Angle(g2,g0) = 0.0862798  'angle'
    c: DistanceX(g2,g2) = 20
FEATURE [PartDesign::CoordinateSystem] Local_CS048
  AttacherType = Attacher::AttachEngine3D
  AttachmentOffset = pos=(0,0,0) rot=(1,0,0;0.099669rad)
  MapMode = 5
  Placement = pos=(0,0,0) rot=(1,0,0;0.099669rad)
  Support = -> [XY_Plane046]
  expr: .AttachmentOffset.Rotation.Roll = Line.AnglePlaneMid
FEATURE [Sketcher::SketchObject] Sketch141
  ExternalGeometry = -> [Line]
  FullyConstrained = false
  MapMode = 5
  Placement = pos=(0,0,0) rot=(1,0,0;0.099669rad)
  Support = -> [Local_CS048]
  expr: Constraints[16] = <<main>>.work_plane_width
  expr: Constraints[4] = (2mm + 0.5mm) * (1 + sin(Line.AnglePlaneMid))
  expr: Support = Local_CS048._self
  sketch-geometry (7):
    g0: LineSegment StartX=171.609 StartY=102.751 StartZ=0 EndX=0 EndY=3.17796 EndZ=0
    g1: LineSegment StartX=0 StartY=3.17796 StartZ=0 EndX=-171.609 EndY=102.751 EndZ=0
    g2: ArcOfCircle CenterX=141.336 CenterY=85.1856 CenterZ=0 NormalX=0 NormalY=0 NormalZ=1 AngleXU=0 Radius=35 StartAngle=0.525756 EndAngle=1.20679
    g3: ArcOfCircle CenterX=-5.31e-14 CenterY=-285.795 CenterZ=0 NormalX=0 NormalY=0 NormalZ=1 AngleXU=0 Radius=431.992 StartAngle=1.20679 EndAngle=1.9348
    g4: ArcOfCircle CenterX=-141.336 CenterY=85.1856 CenterZ=0 NormalX=0 NormalY=0 NormalZ=1 AngleXU=0 Radius=35 StartAngle=1.9348 EndAngle=2.61584
    g5: LineSegment StartX=0 StartY=3.17796 StartZ=0 EndX=-1.37951 EndY=2.37753 EndZ=0
    g6: LineSegment StartX=-1.37951 StartY=2.37753 StartZ=0 EndX=-2e-16 EndY=-1.42e-14 EndZ=0
  constraints (20):
    c: Symmetric(g1,g0,g-2)
    c: PointOnObject(g0,g-2)
    c: Parallel(g0,g-3)
    c: Angle(g-1,g0) = 0.525756
    c: Distance(g-3,g0) = 2.74876
    c: PointOnObject(g2,g0)
    c: Coincident(g2,g0)
    c: Tangent(g2,g3) = -1.5708
    c: PointOnObject(g4,g1)
    c: Coincident(g4,g1)
    c: Tangent(g4,g3) = -1.5708
    c: Equal(g4,g2)
    c: Coincident(g5,g6)
    c: Coincident(g6,g-3)
    c: Perpendicular(g5,g6)
    c: Tangent(g0,g5) = -1.5708
    c: Distance(g0,g5) = 200
    c: Diameter(g2) = 70
    c: Coincident(g1,g0)
    c: DistanceY(g0) = 3.17796  'offset'
FEATURE [PartDesign::Pad] Pad031
  Direction = (0,-0.0995037,0.995037)
  Length = 0.5
  Length2 = 10
  Placement = pos=(0,0,0) rot=(1,0,0;0.099669rad)
  Profile = -> Sketch141
  ReferenceAxis = -> Sketch141 [N_Axis]
  Type = 0
FEATURE [PartDesign::FeaturePython] Bend018  # WARN: FeaturePython — macro-defined, semantics opaque (R4)
  AutoMiter = true
  BaseFeature = -> Pad031
  BendType = 0
  LengthList = [10]
  LengthSpec = 0
  ReliefFactor = 0.7
  UseReliefFactor = false
  angle = 94.9435
  baseObject = -> Pad031 [Edge3,Edge6]
  bendAList = [94.9435]
  extend1 = 0
  extend2 = 0
  gap1 = 0
  gap2 = 0
  invert = false
  kfactor = 0.5
  length = 10
  maxExtendDist = 5
  minGap = 0.1
  minReliefGap = 1
  miterangle1 = 0
  miterangle2 = 0
  offset = 0
  radius = 2
  reliefType = 0
  reliefd = 1
  reliefw = 0.8
  sketchflip = false
  sketchinvert = false
  unfold = false
  expr: angle = 90° + Sketch144.Constraints.angle
FEATURE [PartDesign::FeaturePython] Extend  # WARN: FeaturePython — macro-defined, semantics opaque (R4)
  BaseFeature = -> Bend018
  Offset = 0.02
  Refine = true
  UseSubtraction = false
  baseObject = -> Bend018 [Face24,Face10]
  gap1 = 0
  gap2 = 0
  length = 10
FEATURE [Sketcher::SketchObject] Sketch145
  AttachmentOffset = pos=(0,3.17796,0) rot=(0,0,1;0rad)
  FullyConstrained = true
  MapMode = 5
  Placement = pos=(0,3.16219,0.316219) rot=(1,0,0;0.099669rad)
  Support = -> [Local_CS048]
  expr: .AttachmentOffset.Base.y = Sketch141.Constraints.offset
  expr: Constraints[4] = 180 - 57
  expr: Support = Local_CS048._self
  sketch-geometry (15):
    g0: ArcOfCircle CenterX=0 CenterY=0 CenterZ=0 NormalX=0 NormalY=0 NormalZ=1 AngleXU=0 Radius=5 StartAngle=5.56216 EndAngle=10.1458
    g1: ArcOfCircle CenterX=4.88235 CenterY=-4.291 CenterZ=0 NormalX=0 NormalY=0 NormalZ=1 AngleXU=0 Radius=1.5 StartAngle=2.42057 EndAngle=3.71755
    g2: ArcOfCircle CenterX=-4.88235 CenterY=-4.291 CenterZ=0 NormalX=0 NormalY=0 NormalZ=1 AngleXU=0 Radius=1.5 StartAngle=5.70723 EndAngle=7.00421
    g3: LineSegment StartX=3.62434 StartY=-5.10796 StartZ=0 EndX=5.79596 EndY=-8.45196 EndZ=0
    g4: ArcOfCircle CenterX=4.53795 CenterY=-9.26891 CenterZ=0 NormalX=0 NormalY=0 NormalZ=1 AngleXU=0 Radius=1.5 StartAngle=5.81195 EndAngle=6.85914
    g5: ArcOfCircle CenterX=7.21097 CenterY=-10.6309 CenterZ=0 NormalX=0 NormalY=0 NormalZ=1 AngleXU=0 Radius=1.5 StartAngle=2.67035 EndAngle=3.71756
    g6: ArcOfCircle CenterX=4.69497 CenterY=-12.2648 CenterZ=0 NormalX=0 NormalY=0 NormalZ=1 AngleXU=0 Radius=1.5 StartAngle=5.28835 EndAngle=6.85915
    g7: LineSegment StartX=5.51193 StartY=-13.5228 StartZ=0 EndX=0 EndY=-17.1023 EndZ=0
    g8: LineSegment StartX=5.95297 StartY=-11.4478 StartZ=0 EndX=1.59586 EndY=-4.73849 EndZ=0
    g9: GeomPoint X=4.23697 Y=-8.80544 Z=0
    g10: LineSegment StartX=-3.62434 StartY=-5.10796 StartZ=0 EndX=-5.79596 EndY=-8.45196 EndZ=0
    g11: ArcOfCircle CenterX=-4.69497 CenterY=-12.2648 CenterZ=0 NormalX=0 NormalY=0 NormalZ=1 AngleXU=0 Radius=1.5 StartAngle=2.56563 EndAngle=4.13643
    g12: LineSegment StartX=-5.51193 StartY=-13.5228 StartZ=0 EndX=0 EndY=-17.1023 EndZ=0
    g13: ArcOfCircle CenterX=-7.21097 CenterY=-10.6309 CenterZ=0 NormalX=0 NormalY=0 NormalZ=1 AngleXU=0 Radius=1.5 StartAngle=5.70722 EndAngle=6.75442
    g14: ArcOfCircle CenterX=-4.53795 CenterY=-9.26891 CenterZ=0 NormalX=0 NormalY=0 NormalZ=1 AngleXU=0 Radius=1.5 StartAngle=2.56563 EndAngle=3.61283
  constraints (38):
    c: Coincident(g0,g-1)
    c: Diameter(g0) = 10
    c: Coincident(g2,g0)
    c: PointOnObject(g7,g-2)
    c: Angle(g-1,g3) = 2.14675
    c: Tangent(g4,g3) = 1.5708
    c: Tangent(g5,g4) = 1.5708
    c: Tangent(g1,g0) = 1.5708
    c: Tangent(g3,g1) = -1.5708
    c: Tangent(g6,g5) = 1.5708
    c: Tangent(g7,g6) = 1.5708
    c: Coincident(g8,g5)
    c: Tangent(g6,g8)
    c: Perpendicular(g3,g7)
    c: Equal(g5,g4)
    c: Equal(g6,g5)
    c: Parallel(g8,g3)
    c: Equal(g1,g4)
    c: PointOnObject(g9,g8)
    c: DistanceY(g9) = -8.80544
    c: PointOnObject(g8,g0)
    c: DistanceX(g8) = 1.59586
    c: Distance(g8) = 8
    c: Diameter(g1) = 3
    c: PointOnObject(g4,g8)
    c: Symmetric(g1,g2,g-2)
    c: Equal(g2,g1)
    c: Coincident(g12,g7)
    c: Tangent(g14,g10) = -1.5708
    c: Tangent(g10,g2) = 1.5708
    c: Tangent(g14,g13) = 1.5708
    c: Tangent(g13,g11) = 1.5708
    c: Tangent(g12,g11) = -1.5708
    c: Equal(g13,g14)
    c: Equal(g14,g11)
    c: Equal(g11,g2)
    c: Symmetric(g14,g4,g-2)
    c: Symmetric(g11,g6,g-2)
FEATURE [PartDesign::FeaturePython] CornerRelief  # WARN: FeaturePython — macro-defined, semantics opaque (R4)
  BaseFeature = -> Extend
  ReliefSketch = 4
  Size = 3
  SizeRatio = 1.5
  Sketch = -> Sketch145
  XOffset = 0
  YOffset = 0
  baseObject = -> Extend [Edge6,Edge19]
  kfactor = 0.5
  expr: Sketch = Sketch145._self
FEATURE [Sketcher::SketchObject] Sketch146
  ExternalGeometry = -> [CornerRelief,Sketch141]
  FullyConstrained = false
  MapMode = 5
  Support = -> [XY_Plane046]
  sketch-geometry (1):
    g0: GeomPoint X=-0.835196 Y=2.62109 Z=0
FEATURE [PartDesign::Body] Body001003005003015006
  Group = -> [Local_CS046,Line,Sketch141,Pad031,Bend018,Sketch142,Sketch143,DatumLine,Sketch144,Local_CS047,Extend,Local_CS048,CornerRelief,Sketch145,Sketch146]
  Origin = -> Origin045
  Tip = -> CornerRelief
COMPONENT P12 — recipe-attached ("plexiglass_holder_bottom_tech", modeled in this document).
Construction recipe (the document's own serialized feature program — sketch geometry with constraints, then the solid features built on it; lengths are millimeters unless a unit is written):

FEATURE [PartDesign::CoordinateSystem] LCS_0004
  AttacherType = Attacher::AttachEngine3D
  MapMode = 2
  Support = -> [X_Axis034]
FEATURE [Sketcher::SketchObject] Sketch101
  FullyConstrained = false
  MapMode = 5
  Support = -> [XY_Plane035]
  sketch-geometry (12):
    g0: LineSegment StartX=1.06e-14 StartY=173.684 StartZ=0 EndX=1.21e-14 EndY=196.875 EndZ=0
    g1: LineSegment StartX=0 StartY=0 StartZ=0 EndX=170.499 EndY=98.4377 EndZ=0
    g2: ArcOfCircle CenterX=0 CenterY=0 CenterZ=0 NormalX=0 NormalY=0 NormalZ=1 AngleXU=0 Radius=173.684 StartAngle=0.625357 EndAngle=1.5708
    g3: ArcOfCircle CenterX=0 CenterY=0 CenterZ=0 NormalX=0 NormalY=0 NormalZ=1 AngleXU=0 Radius=196.875 StartAngle=0.763183 EndAngle=1.5708
    g4: LineSegment StartX=142.27 StartY=136.085 StartZ=0 EndX=150.91 EndY=127.052 EndZ=0
    g5: LineSegment StartX=150.91 StartY=127.052 StartZ=0 EndX=159.551 EndY=118.019 EndZ=0
    g6: LineSegment StartX=146.574 StartY=122.905 StartZ=0 EndX=150.91 EndY=127.052 EndZ=0
    g7: LineSegment StartX=150.91 StartY=127.052 StartZ=0 EndX=158.859 EndY=118.742 EndZ=0
    g8: ArcOfCircle CenterX=158.137 CenterY=118.051 CenterZ=0 NormalX=0 NormalY=0 NormalZ=1 AngleXU=0 Radius=1 StartAngle=5.47557 EndAngle=7.04637
    g9: LineSegment StartX=158.828 StartY=117.328 StartZ=0 EndX=142.317 EndY=101.535 EndZ=0
    g10: ArcOfCircle CenterX=141.626 CenterY=102.258 CenterZ=0 NormalX=0 NormalY=0 NormalZ=1 AngleXU=0 Radius=1 StartAngle=3.76695 EndAngle=5.47557
    g11: GeomPoint X=141.485 Y=100.739 Z=0
  constraints (31):
    c: PointOnObject(g0,g-2)
    c: PointOnObject(g0,g-2)
    c: Coincident(g2,g0)
    c: Coincident(g3,g0)
    c: Angle(g-1,g1) = 0.523599
    c: DistanceY(g0) = 196.875  'r'
    c: Coincident(g2,g-1)
    c: Coincident(g2,g1)
    c: Coincident(g5,g4)
    c: Parallel(g4,g5)
    c: Equal(g4,g5)
    c: Tangent(g4,g3) = 1.5708
    c: Coincident(g6,g4)
    c: Perpendicular(g6,g4)
    c: Distance(g5,g3) = 25
    c: Coincident(g3,g2)
    c: Coincident(g7,g4)
    c: PointOnObject(g7,g5)
    c: PointOnObject(g5,g9)
    c: Tangent(g9,g8) = 1.5708
    c: Perpendicular(g5,g9)
    c: Tangent(g10,g9) = 1.5708
    c: Tangent(g10,g2) = 1.5708
    c: Equal(g10,g8)
    c: Diameter(g10) = 2
    c: Tangent(g8,g7) = 1.5708
    c: PointOnObject(g11,g9)
    c: PointOnObject(g11,g2)
    c: Distance(g11,g5) = 25
    c: DistanceY(g0,g0) = 23.1913
    c: Distance(g6) = 6
FEATURE [PartDesign::Pad] Pad026
  Direction = (0,0,1)
  Length = 3
  Length2 = 10
  Profile = -> Sketch101
  ReferenceAxis = -> Sketch101 [N_Axis]
  Type = 0
FEATURE [PartDesign::SubShapeBinder] Binder039
  BindCopyOnChange = 0
  BindMode = 0
  ClaimChildren = false
  Context = -> Body_6 [Binder039.]
  Fuse = false
  MakeFace = true
  OffsetFill = false
  OffsetIntersection = false
  OffsetJoinType = 0
  OffsetOpenResult = false
  PartialLoad = false
  Relative = true
  Support = -> [Body001003005003014[Binder038.]]
  _Version = 2
FEATURE [PartDesign::Pocket] Pocket058
  BaseFeature = -> Pad026
  Direction = (0,0,-1)
  Length = 5
  Length2 = 5
  Midplane = true
  Profile = -> Binder039
  Type = 1
FEATURE [PartDesign::Mirrored] Mirrored037
  BaseFeature = -> Pocket058
  MirrorPlane = -> Sketch101 [V_Axis]
  Originals = -> [Pad026,Pocket058]
  Refine = true
FEATURE [PartDesign::SubShapeBinder] Binder040
  BindCopyOnChange = 0
  BindMode = 0
  ClaimChildren = false
  Context = -> Body_6 [Binder040.]
  Fuse = false
  MakeFace = true
  OffsetFill = false
  OffsetIntersection = false
  OffsetJoinType = 0
  OffsetOpenResult = false
  PartialLoad = false
  Placement = pos=(0,196.875,0) rot=(0,0,1;3.14159rad)
  Relative = true
  Support = -> [tech_mid[Pocket076.Sketch123.]]
  _Version = 2
FEATURE [PartDesign::Pocket] Pocket078
  BaseFeature = -> Mirrored037
  Direction = (0,0,-1)
  Length = 5
  Length2 = 5
  Midplane = true
  Profile = -> Binder040
  Type = 1
FEATURE [PartDesign::Body] Body_6  label="plexiglass_holder_bottom_tech"
  Group = -> [LCS_0004,Sketch101,Pad026,Pocket058,Mirrored037,Binder039,Binder040,Pocket078]
  Origin = -> Origin034
  Tip = -> Pocket078
COMPONENT P13 — recipe-attached ("ugol_mini_material_0.30ansi", modeled in this document).
Construction recipe (the document's own serialized feature program — sketch geometry with constraints, then the solid features built on it; lengths are millimeters unless a unit is written):

FEATURE [PartDesign::CoordinateSystem] LCS_0005
  AttacherType = Attacher::AttachEngine3D
  MapMode = 2
  Support = -> [X_Axis035]
FEATURE [Sketcher::SketchObject] Sketch104
  FullyConstrained = false
  MapMode = 5
  Placement = pos=(0,0,0) rot=(0.57735,0.57735,0.57735;2.0944rad)
  Support = -> [YZ_Plane035]
  sketch-geometry (3):
    g0: LineSegment StartX=10.9 StartY=0 StartZ=0 EndX=0 EndY=0 EndZ=0
    g1: LineSegment StartX=0 StartY=0 StartZ=0 EndX=0 EndY=17.2 EndZ=0
    g2: GeomPoint X=12.5 Y=0 Z=0
  constraints (7):
    c: PointOnObject(g0,g-1)
    c: Coincident(g0,g-1)
    c: Coincident(g0,g1)
    c: PointOnObject(g1,g-2)
    c: PointOnObject(g2,g-1)
    c: DistanceY(g1) = 17.2
    c: DistanceX(g0,g0) = 10.9
FEATURE [PartDesign::FeaturePython] BaseBend006  # WARN: FeaturePython — macro-defined, semantics opaque (R4)
  BendSide = 0
  BendSketch = -> Sketch104
  MidPlane = true
  Reverse = false
  length = 9.4
  radius = 2
  thickness = 0.5
FEATURE [Sketcher::SketchObject] Sketch105
  AttachmentOffset = pos=(0,5.9,0) rot=(0,0,1;0rad)
  FullyConstrained = true
  MapMode = 5
  Placement = pos=(0,5.9,0) rot=(0,0,1;0rad)
  Support = -> [XY_Plane036]
  sketch-geometry (1):
    g0: Circle CenterX=0 CenterY=0 CenterZ=0 NormalX=0 NormalY=0 NormalZ=1 AngleXU=0 Radius=1.7
  constraints (2):
    c: Coincident(g0,g-1)
    c: Diameter(g0) = 3.4
FEATURE [PartDesign::Plane] DatumPlane024
  AttachmentOffset = pos=(0,0,0) rot=(1,0,0;0.785398rad)
  Length = 61.8921
  MapMode = 5
  Placement = pos=(0,0,0) rot=(1,0,0;0.785398rad)
  ResizeMode = 0
  Support = -> [XY_Plane036]
  Width = 82.6027
FEATURE [PartDesign::Fillet] Fillet002
  Base = -> BaseBend006 [Edge25,Edge8]
  BaseFeature = -> BaseBend006
  Radius = 2
  SupportTransform = false
  UseAllEdges = false
FEATURE [PartDesign::Mirrored] Mirrored038
  BaseFeature = -> Fillet002
  MirrorPlane = -> YZ_Plane035
  Originals = -> [Fillet002]
FEATURE [PartDesign::Pocket] Pocket061
  BaseFeature = -> Mirrored038
  Direction = (0,0,-1)
  Length = 5
  Length2 = 5
  Midplane = true
  Profile = -> Sketch105
  ReferenceAxis = -> Sketch105 [N_Axis]
  Type = 1
FEATURE [Sketcher::SketchObject] Sketch106
  AttachmentOffset = pos=(0,12.5,0) rot=(0,0,1;0rad)
  FullyConstrained = true
  MapMode = 5
  Placement = pos=(0,-2.8e-15,12.5) rot=(1,0,0;1.5708rad)
  Support = -> [XZ_Plane035]
  sketch-geometry (1):
    g0: Circle CenterX=0 CenterY=0 CenterZ=0 NormalX=0 NormalY=0 NormalZ=1 AngleXU=0 Radius=1.7
  constraints (2):
    c: Coincident(g0,g-1)
    c: Diameter(g0) = 3.4
FEATURE [PartDesign::Pocket] Pocket062
  BaseFeature = -> Pocket061
  Direction = (0,1,2e-16)
  Length = 5
  Length2 = 5
  Midplane = true
  Profile = -> Sketch106
  ReferenceAxis = -> Sketch106 [N_Axis]
  Type = 1
FEATURE [PartDesign::Body] Body_7  label="ugol_mini_material_0.30ansi"
  Group = -> [LCS_0005,Sketch104,BaseBend006,Sketch105,DatumPlane024,Fillet002,Mirrored038,Pocket061,Sketch106,Pocket062]
  Origin = -> Origin035
  Tip = -> Pocket062
COMPONENT P14 — recipe-attached ("gutter_bottom_material_0.30ansi", modeled in this document).
Construction recipe (the document's own serialized feature program — sketch geometry with constraints, then the solid features built on it; lengths are millimeters unless a unit is written):

FEATURE [Sketcher::SketchObject] Sketch134
  FullyConstrained = true
  MapMode = 5
  Placement = pos=(0,0,0) rot=(1,0,0;1.5708rad)
  Support = -> [XZ_Plane044]
  sketch-geometry (5):
    g0: LineSegment StartX=-8.5 StartY=15 StartZ=0 EndX=-8.5 EndY=0 EndZ=0
    g1: LineSegment StartX=-8.5 StartY=0 StartZ=0 EndX=8.5 EndY=0 EndZ=0
    g2: LineSegment StartX=8.5 StartY=0 StartZ=0 EndX=8.5 EndY=15 EndZ=0
    g3: LineSegment StartX=8.5 StartY=15 StartZ=0 EndX=-8.5 EndY=15 EndZ=0
    g4: GeomPoint X=0 Y=7.5 Z=0
  constraints (13):
    c: Coincident(g0,g1)
    c: Coincident(g1,g2)
    c: Coincident(g2,g3)
    c: Coincident(g3,g0)
    c: Horizontal(g1)
    c: Horizontal(g3)
    c: Vertical(g0)
    c: Vertical(g2)
    c: Symmetric(g1,g0,g4)
    c: PointOnObject(g4,g-2)
    c: PointOnObject(g1,g-1)
    c: DistanceX(g1,g1) = 17  'width'
    c: DistanceY(g2) = 15  'height'
FEATURE [Sketcher::SketchObject] Sketch135
  FullyConstrained = true
  MapMode = 5
  Placement = pos=(0,0,0) rot=(1,0,0;1.5708rad)
  Support = -> [XZ_Plane044]
  sketch-geometry (1):
    g0: GeomPoint X=172 Y=45 Z=0
  constraints (3):
    c: DistanceX(g0) = 172
    c: DistanceY(g0) = 45
    c: Distance(g-1,g0) = 177.789  'length'
FEATURE [PartDesign::FeaturePython] BaseBend010  # WARN: FeaturePython — macro-defined, semantics opaque (R4)
  BendSide = 0
  BendSketch = -> Sketch134
  MidPlane = true
  Reverse = false
  length = 187.789
  radius = 0.1
  thickness = 0.3
FEATURE [Sketcher::SketchObject] Sketch136
  AttachmentOffset = pos=(0,8,0) rot=(0,0,1;0rad)
  FullyConstrained = true
  MapMode = 5
  Placement = pos=(-1.8e-15,1.8e-15,8) rot=(0.57735,0.57735,0.57735;2.0944rad)
  Support = -> [YZ_Plane044]
  sketch-geometry (2):
    g0: Circle CenterX=-88.8946 CenterY=0 CenterZ=0 NormalX=0 NormalY=0 NormalZ=1 AngleXU=0 Radius=1.7
    g1: Circle CenterX=88.8946 CenterY=0 CenterZ=0 NormalX=0 NormalY=0 NormalZ=1 AngleXU=0 Radius=1.7
  constraints (5):
    c: PointOnObject(g0,g-1)
    c: Symmetric(g0,g1,g-2)
    c: DistanceX(g0,g1) = 177.789
    c: Equal(g1,g0)
    c: Diameter(g1) = 3.4
FEATURE [Sketcher::SketchObject] Sketch137
  AttachmentOffset = pos=(93.8946,15,0) rot=(0,0,1;0rad)
  FullyConstrained = true
  MapMode = 5
  Placement = pos=(1.75e-14,93.8946,15) rot=(0.57735,0.57735,0.57735;2.0944rad)
  Support = -> [YZ_Plane044]
  sketch-geometry (3):
    g0: ArcOfCircle CenterX=-7 CenterY=-7 CenterZ=0 NormalX=0 NormalY=0 NormalZ=1 AngleXU=0 Radius=7 StartAngle=-3.2e-14 EndAngle=1.5708
    g1: LineSegment StartX=-7 StartY=0 StartZ=0 EndX=0 EndY=0 EndZ=0
    g2: LineSegment StartX=0 StartY=0 StartZ=0 EndX=0 EndY=-7 EndZ=0
  constraints (8):
    c: PointOnObject(g0,g-2)
    c: PointOnObject(g0,g-1)
    c: Coincident(g1,g2)
    c: Vertical(g2)
    c: Tangent(g2,g0) = 1.5708
    c: Tangent(g0,g1) = 1.5708
    c: DistanceY(g2,g2) = 7
    c: Horizontal(g1)
FEATURE [PartDesign::Pocket] Pocket092
  BaseFeature = -> BaseBend010
  Direction = (-1,2e-16,-3e-16)
  Length = 5
  Length2 = 5
  Midplane = true
  Profile = -> Sketch137
  ReferenceAxis = -> Sketch137 [N_Axis]
  Type = 1
FEATURE [PartDesign::Mirrored] Mirrored041
  BaseFeature = -> Pocket092
  MirrorPlane = -> XZ_Plane044
  Originals = -> [Pocket092]
FEATURE [Sketcher::SketchObject] Sketch138
  AttachmentOffset = pos=(0,-63.8946,0) rot=(0,0,1;0rad)
  FullyConstrained = false
  MapMode = 5
  Placement = pos=(0,-63.8946,0) rot=(0,0,1;0rad)
  Support = -> [XY_Plane045]
  sketch-geometry (5):
    g0: LineSegment StartX=-8.25 StartY=-159.942 StartZ=0 EndX=-8.25 EndY=0 EndZ=0
    g1: LineSegment StartX=-8.25 StartY=0 StartZ=0 EndX=8.25 EndY=0 EndZ=0
    g2: LineSegment StartX=8.25 StartY=0 StartZ=0 EndX=8.25 EndY=-159.942 EndZ=0
    g3: LineSegment StartX=8.25 StartY=-159.942 StartZ=0 EndX=-8.25 EndY=-159.942 EndZ=0
    g4: GeomPoint X=0 Y=-79.9711 Z=0
  constraints (12):
    c: Coincident(g0,g1)
    c: Coincident(g1,g2)
    c: Coincident(g2,g3)
    c: Coincident(g3,g0)
    c: Horizontal(g1)
    c: Horizontal(g3)
    c: Vertical(g0)
    c: Vertical(g2)
    c: Symmetric(g1,g0,g4)
    c: PointOnObject(g4,g-2)
    c: PointOnObject(g1,g-1)
    c: DistanceX(g1,g1) = 16.5
FEATURE [PartDesign::Pocket] Pocket093
  BaseFeature = -> Mirrored041
  Direction = (0,0,-1)
  Length = 5
  Length2 = 5
  Profile = -> Sketch138
  ReferenceAxis = -> Sketch138 [N_Axis]
  Type = 1
FEATURE [Sketcher::SketchObject] Sketch139
  AttachmentOffset = pos=(-93.8946,0,0) rot=(0,0,1;0rad)
  FullyConstrained = true
  MapMode = 5
  Placement = pos=(-2.08e-14,-93.8946,2.08e-14) rot=(0.57735,0.57735,0.57735;2.0944rad)
  Support = -> [YZ_Plane044]
  sketch-geometry (4):
    g0: ArcOfCircle CenterX=5 CenterY=5.1 CenterZ=0 NormalX=0 NormalY=0 NormalZ=1 AngleXU=0 Radius=5 StartAngle=3.14159 EndAngle=4.71239
    g1: LineSegment StartX=0 StartY=5.1 StartZ=0 EndX=0 EndY=-0.3 EndZ=0
    g2: LineSegment StartX=0 StartY=-0.3 StartZ=0 EndX=5 EndY=-0.3 EndZ=0
    g3: LineSegment StartX=5 StartY=-0.3 StartZ=0 EndX=5 EndY=0.1 EndZ=0
  constraints (12):
    c: PointOnObject(g0,g-2)
    c: PointOnObject(g1,g-2)
    c: Coincident(g2,g1)
    c: Horizontal(g2)
    c: Coincident(g3,g2)
    c: Coincident(g3,g0)
    c: Vertical(g3)
    c: Perpendicular(g0,g3)
    c: Tangent(g1,g0) = -1.5708
    c: DistanceY(g0) = 0.1
    c: Diameter(g0) = 10
    c: DistanceY(g1) = -0.3
FEATURE [PartDesign::Pocket] Pocket094
  BaseFeature = -> Pocket093
  Direction = (-1,2e-16,-3e-16)
  Length = 5
  Length2 = 5
  Midplane = true
  Profile = -> Sketch139
  ReferenceAxis = -> Sketch139 [N_Axis]
  Type = 1
FEATURE [Sketcher::SketchObject] Sketch140
  FullyConstrained = true
  MapMode = 5
  Placement = pos=(0,0,0) rot=(0.57735,0.57735,0.57735;2.0944rad)
  Support = -> [YZ_Plane044]
  sketch-geometry (4):
    g0: LineSegment StartX=-163.895 StartY=-10 StartZ=0 EndX=-63.8946 EndY=-10 EndZ=0
    g1: LineSegment StartX=-63.8946 StartY=-10 StartZ=0 EndX=-63.8946 EndY=0.11 EndZ=0
    g2: LineSegment StartX=-63.8946 StartY=0.11 StartZ=0 EndX=-163.895 EndY=0.11 EndZ=0
    g3: LineSegment StartX=-163.895 StartY=0.11 StartZ=0 EndX=-163.895 EndY=-10 EndZ=0
  constraints (12):
    c: Coincident(g0,g1)
    c: Coincident(g1,g2)
    c: Coincident(g2,g3)
    c: Coincident(g3,g0)
    c: Horizontal(g0)
    c: Horizontal(g2)
    c: Vertical(g1)
    c: Vertical(g3)
    c: DistanceY(g2) = 0.11
    c: DistanceX(g1) = -63.8946
    c: DistanceY(g0) = -10
    c: DistanceX(g2,g2) = 100
FEATURE [PartDesign::Pocket] Pocket095
  BaseFeature = -> Pocket094
  Direction = (-1,2e-16,-3e-16)
  Length = 5
  Length2 = 5
  Midplane = true
  Profile = -> Sketch140
  ReferenceAxis = -> Sketch140 [N_Axis]
  Type = 1
FEATURE [PartDesign::Pocket] Pocket091
  BaseFeature = -> Pocket095
  Direction = (-1,2e-16,-3e-16)
  Length = 5
  Length2 = 5
  Midplane = true
  Profile = -> Sketch136
  ReferenceAxis = -> Sketch136 [N_Axis]
  Type = 1
FEATURE [PartDesign::Body] gutter_bottom  label="gutter_bottom_material_0.30ansi"
  Group = -> [Sketch134,Sketch135,BaseBend010,Sketch136,Sketch137,Pocket092,Mirrored041,Sketch138,Pocket093,Sketch139,Pocket094,Sketch140,Pocket095,Pocket091]
  Origin = -> Origin044
  Tip = -> Pocket091
COMPONENT P15 — recipe-attached ("tech_mid_material_0.50ansi", modeled in this document).
Construction recipe (the document's own serialized feature program — sketch geometry with constraints, then the solid features built on it; lengths are millimeters unless a unit is written):

FEATURE [PartDesign::CoordinateSystem] LCS_0007
  AttacherType = Attacher::AttachEngine3D
  MapMode = 2
  Support = -> [X_Axis038]
FEATURE [Sketcher::SketchObject] Sketch122
  FullyConstrained = true
  MapMode = 5
  Placement = pos=(0,0,0) rot=(0.57735,0.57735,0.57735;2.0944rad)
  Support = -> [YZ_Plane038]
  sketch-geometry (4):
    g0: LineSegment StartX=0 StartY=0 StartZ=0 EndX=15 EndY=0 EndZ=0
    g1: LineSegment StartX=15 StartY=0 StartZ=0 EndX=15 EndY=151 EndZ=0
    g2: LineSegment StartX=15 StartY=151 StartZ=0 EndX=0 EndY=151 EndZ=0
    g3: LineSegment StartX=0 StartY=151 StartZ=0 EndX=0 EndY=0 EndZ=0
  constraints (11):
    c: Coincident(g0,g1)
    c: Coincident(g1,g2)
    c: Coincident(g2,g3)
    c: Coincident(g3,g0)
    c: Horizontal(g0)
    c: Horizontal(g2)
    c: Vertical(g1)
    c: Vertical(g3)
    c: Coincident(g0,g-1)
    c: DistanceY(g2) = 151  'height'
    c: DistanceX(g0,g0) = 15  'length'
FEATURE [PartDesign::FeaturePython] BaseBend009  # WARN: FeaturePython — macro-defined, semantics opaque (R4)
  BendSide = 1
  BendSketch = -> Sketch122
  MidPlane = true
  Reverse = false
  length = 10
  radius = 0.1
  thickness = 0.3
FEATURE [Sketcher::SketchObject] Sketch123
  FullyConstrained = true
  MapMode = 5
  Support = -> [XY_Plane039]
  sketch-geometry (3):
    g0: Circle CenterX=0 CenterY=7.5 CenterZ=0 NormalX=0 NormalY=0 NormalZ=1 AngleXU=0 Radius=1.7
    g1: LineSegment StartX=0 StartY=0 StartZ=0 EndX=0 EndY=7.5 EndZ=0
    g2: LineSegment StartX=0 StartY=7.5 StartZ=0 EndX=0 EndY=15 EndZ=0
  constraints (8):
    c: PointOnObject(g0,g-2)
    c: Diameter(g0) = 3.4
    c: Coincident(g1,g-1)
    c: Coincident(g1,g0)
    c: Coincident(g2,g0)
    c: PointOnObject(g2,g-2)
    c: Equal(g2,g1)
    c: DistanceY(g2) = 15
FEATURE [PartDesign::Pocket] Pocket076
  BaseFeature = -> BaseBend009
  Direction = (0,0,-1)
  Length = 5
  Length2 = 5
  Midplane = true
  Profile = -> Sketch123
  ReferenceAxis = -> Sketch123 [N_Axis]
  Type = 1
FEATURE [Sketcher::SketchObject] Sketch124
  FullyConstrained = true
  MapMode = 5
  Placement = pos=(0,0,0) rot=(1,0,0;1.5708rad)
  Support = -> [XZ_Plane038]
  sketch-geometry (2):
    g0: Circle CenterX=0 CenterY=75.5 CenterZ=0 NormalX=0 NormalY=0 NormalZ=1 AngleXU=0 Radius=1.7
    g1: GeomPoint X=0 Y=151 Z=0
  constraints (4):
    c: PointOnObject(g0,g-2)
    c: DistanceY(g1) = 151
    c: Symmetric(g1,g-1,g0)
    c: Diameter(g0) = 3.4
FEATURE [PartDesign::Pocket] Pocket077
  BaseFeature = -> Pocket076
  Direction = (0,1,2e-16)
  Length = 5
  Length2 = 5
  Midplane = true
  Profile = -> Sketch124
  ReferenceAxis = -> Sketch124 [N_Axis]
  Type = 1
FEATURE [PartDesign::Body] tech_mid  label="tech_mid_material_0.50ansi"
  Group = -> [LCS_0007,Sketch122,BaseBend009,Sketch123,Pocket076,Sketch124,Pocket077]
  Origin = -> Origin038
  Tip = -> Pocket077
